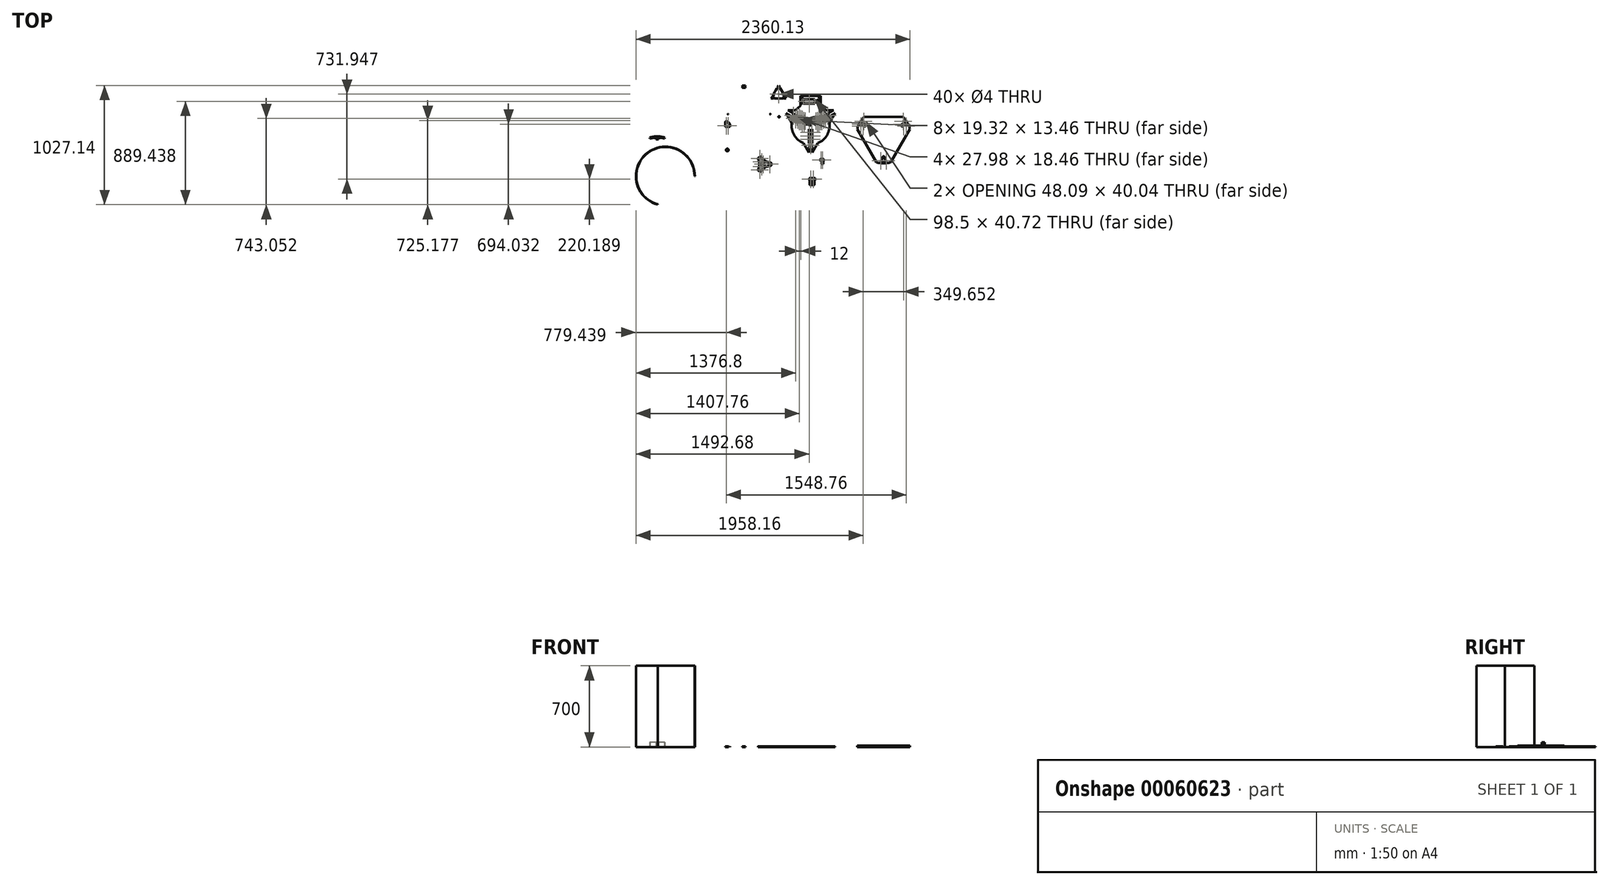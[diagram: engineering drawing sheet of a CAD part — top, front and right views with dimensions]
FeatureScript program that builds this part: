
annotation { "Feature Type Name" : "Feature", "Feature Type Description" : "" }
export const myFeature = defineFeature(function(context is Context, id is Id, definition is map)
    precondition{}
    {
        {
            var Q0;
            Q0=qCreatedBy(makeId("Top.planeOp"),FACE);
            var sketch = newSketch(context, id + "F0", { "sketchPlane" : qUnion([Q0])});
            skCircle(sketch, "E0", {"center": v(-448.83, 54.99) * mm, "radius": 1.5 * mm});
            skCircle(sketch, "E1", {"center": v(-448.8, 86.08) * mm, "radius": 1.5 * mm});
            skCircle(sketch, "E2", {"center": v(-453.84, -253.52) * mm, "radius": 11.5 * mm});
            skCircle(sketch, "E3", {"center": v(-386.12, -280.64) * mm, "radius": 2 * mm});
            skCircle(sketch, "E4", {"center": v(-423.42, -280.64) * mm, "radius": 2 * mm});
            skCircle(sketch, "E5", {"center": v(-469.5, -280.64) * mm, "radius": 2 * mm});
            skCircle(sketch, "E6", {"center": v(-438.44, -237.96) * mm, "radius": 1.5 * mm});
            skCircle(sketch, "E7", {"center": v(-469.53, -237.9) * mm, "radius": 1.5 * mm});
            skCircle(sketch, "E8", {"center": v(-439.73, -262.53) * mm, "radius": 1.5 * mm});
            skCircle(sketch, "E9", {"center": v(-448.28, -269) * mm, "radius": 1.5 * mm});
            skCircle(sketch, "E10", {"center": v(-438.44, -291.39) * mm, "radius": 1.5 * mm});
            skCircle(sketch, "E11", {"center": v(-469.55, -291.39) * mm, "radius": 1.5 * mm});
            skCircle(sketch, "E12", {"center": v(-469.55, -269) * mm, "radius": 1.5 * mm});
            skCircle(sketch, "E13", {"center": v(-83.7, 56.02) * mm, "radius": 2 * mm});
            skCircle(sketch, "E14", {"center": v(-231.13, -199.23) * mm, "radius": 2 * mm});
            skCircle(sketch, "E15", {"center": v(-378.53, 55.85) * mm, "radius": 2 * mm});
            skCircle(sketch, "E16", {"center": v(-231.13, -29.98) * mm, "radius": 177.5 * mm});
            skLineSegment(sketch, "E17", {"start": v(-11.84, 302.96) * mm, "end": v(-1.84, 285.64) * mm});
            skLineSegment(sketch, "E18", {"start": v(-1.84, 285.64) * mm, "end": v(-1.84, 258.8) * mm});
            skLineSegment(sketch, "E19", {"start": v(-1.84, 258.8) * mm, "end": v(2.16, 258.8) * mm});
            skLineSegment(sketch, "E20", {"start": v(2.16, 258.8) * mm, "end": v(2.16, 278.7) * mm});
            skLineSegment(sketch, "E21", {"start": v(2.16, 278.7) * mm, "end": v(39.1, 214.7) * mm});
            skLineSegment(sketch, "E22", {"start": v(39.1, 214.7) * mm, "end": v(21.87, 224.66) * mm});
            skLineSegment(sketch, "E23", {"start": v(21.87, 224.66) * mm, "end": v(19.87, 221.2) * mm});
            skLineSegment(sketch, "E24", {"start": v(19.87, 221.2) * mm, "end": v(43.1, 207.78) * mm});
            skLineSegment(sketch, "E25", {"start": v(43.1, 207.78) * mm, "end": v(53.1, 190.46) * mm});
            skLineSegment(sketch, "E26", {"start": v(53.1, 190.46) * mm, "end": v(33.1, 190.46) * mm});
            skLineSegment(sketch, "E27", {"start": v(33.1, 190.46) * mm, "end": v(9.87, 203.88) * mm});
            skLineSegment(sketch, "E28", {"start": v(9.87, 203.88) * mm, "end": v(7.87, 200.41) * mm});
            skLineSegment(sketch, "E29", {"start": v(7.87, 200.41) * mm, "end": v(25.1, 190.46) * mm});
            skLineSegment(sketch, "E30", {"start": v(25.1, 190.46) * mm, "end": v(-48.8, 190.46) * mm});
            skLineSegment(sketch, "E31", {"start": v(-48.8, 190.46) * mm, "end": v(-31.55, 200.41) * mm});
            skLineSegment(sketch, "E32", {"start": v(-31.55, 200.41) * mm, "end": v(-33.55, 203.88) * mm});
            skLineSegment(sketch, "E33", {"start": v(-33.55, 203.88) * mm, "end": v(-56.8, 190.46) * mm});
            skLineSegment(sketch, "E34", {"start": v(-56.8, 190.46) * mm, "end": v(-76.8, 190.46) * mm});
            skLineSegment(sketch, "E35", {"start": v(-76.8, 190.46) * mm, "end": v(-66.8, 207.78) * mm});
            skLineSegment(sketch, "E36", {"start": v(-66.8, 207.78) * mm, "end": v(-43.55, 221.2) * mm});
            skLineSegment(sketch, "E37", {"start": v(-43.55, 221.2) * mm, "end": v(-45.55, 224.66) * mm});
            skLineSegment(sketch, "E38", {"start": v(-45.55, 224.66) * mm, "end": v(-62.8, 214.7) * mm});
            skLineSegment(sketch, "E39", {"start": v(-62.8, 214.7) * mm, "end": v(-25.84, 278.7) * mm});
            skLineSegment(sketch, "E40", {"start": v(-25.84, 278.7) * mm, "end": v(-25.84, 258.8) * mm});
            skLineSegment(sketch, "E41", {"start": v(-25.84, 258.8) * mm, "end": v(-21.84, 258.8) * mm});
            skLineSegment(sketch, "E42", {"start": v(-21.84, 258.8) * mm, "end": v(-21.84, 285.64) * mm});
            skLineSegment(sketch, "E43", {"start": v(-21.84, 285.64) * mm, "end": v(-11.84, 302.96) * mm});
            skLineSegment(sketch, "E44", {"start": v(-314.86, 291.44) * mm, "end": v(-314.86, 289.44) * mm});
            skLineSegment(sketch, "E45", {"start": v(-314.86, 289.44) * mm, "end": v(-318.06, 289.45) * mm});
            skLineSegment(sketch, "E46", {"start": v(-318.06, 289.45) * mm, "end": v(-318.06, 291.45) * mm});
            skLineSegment(sketch, "E47", {"start": v(-318.06, 291.45) * mm, "end": v(-321.05, 291.44) * mm});
            skLineSegment(sketch, "E48", {"start": v(-321.05, 291.44) * mm, "end": v(-321.05, 287.57) * mm});
            skLineSegment(sketch, "E49", {"start": v(-325, 287.57) * mm, "end": v(-325, 282.96) * mm});
            skLineSegment(sketch, "E50", {"start": v(-314.88, 291.44) * mm, "end": v(-314.86, 291.44) * mm});
            skLineSegment(sketch, "E51", {"start": v(-314.86, 291.44) * mm, "end": v(-312.83, 291.44) * mm});
            skLineSegment(sketch, "E52", {"start": v(-312.83, 291.44) * mm, "end": v(-312.83, 294.44) * mm});
            skLineSegment(sketch, "E53", {"start": v(-312.83, 294.44) * mm, "end": v(-314.81, 294.44) * mm});
            skLineSegment(sketch, "E54", {"start": v(-314.81, 294.44) * mm, "end": v(-314.86, 294.44) * mm});
            skLineSegment(sketch, "E55", {"start": v(-314.86, 294.44) * mm, "end": v(-314.86, 296.44) * mm});
            skLineSegment(sketch, "E56", {"start": v(-314.86, 296.44) * mm, "end": v(-318.06, 296.45) * mm});
            skLineSegment(sketch, "E57", {"start": v(-318.06, 296.45) * mm, "end": v(-318.06, 294.44) * mm});
            skLineSegment(sketch, "E58", {"start": v(-318.06, 294.44) * mm, "end": v(-321.05, 294.44) * mm});
            skLineSegment(sketch, "E59", {"start": v(-321.05, 294.44) * mm, "end": v(-321.05, 298.32) * mm});
            skLineSegment(sketch, "E60", {"start": v(-321.05, 298.32) * mm, "end": v(-325, 298.32) * mm});
            skLineSegment(sketch, "E61", {"start": v(-325, 298.32) * mm, "end": v(-325, 302.96) * mm});
            skLineSegment(sketch, "E62", {"start": v(-461.5, -205.94) * mm, "end": v(-452.17, -195.94) * mm});
            skLineSegment(sketch, "E63", {"start": v(-452.17, -195.94) * mm, "end": v(-452, -195.94) * mm});
            skLineSegment(sketch, "E64", {"start": v(-452, -195.94) * mm, "end": v(-451.98, -195.73) * mm});
            skLineSegment(sketch, "E65", {"start": v(-451.98, -195.73) * mm, "end": v(-447.3, -190.7) * mm});
            skLineSegment(sketch, "E66", {"start": v(-447.3, -190.7) * mm, "end": v(-442.5, -195.94) * mm});
            skLineSegment(sketch, "E67", {"start": v(-442.5, -195.94) * mm, "end": v(-452, -205.94) * mm});
            skLineSegment(sketch, "E68", {"start": v(-452, -205.94) * mm, "end": v(-461.5, -205.94) * mm});
            skLineSegment(sketch, "E69", {"start": v(-442.5, -144.44) * mm, "end": v(-447.25, -149.62) * mm});
            skLineSegment(sketch, "E70", {"start": v(-447.25, -149.62) * mm, "end": v(-456.75, -149.62) * mm});
            skLineSegment(sketch, "E71", {"start": v(-456.75, -149.62) * mm, "end": v(-461.5, -144.44) * mm});
            skLineSegment(sketch, "E72", {"start": v(-461.5, -144.44) * mm, "end": v(-452, -144.44) * mm});
            skLineSegment(sketch, "E73", {"start": v(-452, -144.44) * mm, "end": v(-461.5, -134.44) * mm});
            skLineSegment(sketch, "E74", {"start": v(-461.5, -134.44) * mm, "end": v(-456.7, -129.2) * mm});
            skLineSegment(sketch, "E75", {"start": v(-456.7, -129.2) * mm, "end": v(-442.5, -144.44) * mm});
            skLineSegment(sketch, "E76", {"start": v(-442.5, -113.69) * mm, "end": v(-447.3, -118.92) * mm});
            skLineSegment(sketch, "E77", {"start": v(-447.3, -118.92) * mm, "end": v(-461.5, -103.69) * mm});
            skLineSegment(sketch, "E78", {"start": v(-461.5, -103.69) * mm, "end": v(-451.82, -103.69) * mm});
            skLineSegment(sketch, "E79", {"start": v(-451.82, -103.69) * mm, "end": v(-442.5, -113.69) * mm});
            skLineSegment(sketch, "E80", {"start": v(-461.5, -175.19) * mm, "end": v(-452, -165.19) * mm});
            skLineSegment(sketch, "E81", {"start": v(-452, -165.19) * mm, "end": v(-461.5, -165.19) * mm});
            skLineSegment(sketch, "E82", {"start": v(-461.5, -165.19) * mm, "end": v(-456.75, -160) * mm});
            skLineSegment(sketch, "E83", {"start": v(-456.75, -160) * mm, "end": v(-447.34, -160) * mm});
            skLineSegment(sketch, "E84", {"start": v(-447.34, -160) * mm, "end": v(-442.67, -165.19) * mm});
            skLineSegment(sketch, "E85", {"start": v(-442.67, -165.19) * mm, "end": v(-456.73, -180.4) * mm});
            skLineSegment(sketch, "E86", {"start": v(-456.73, -180.4) * mm, "end": v(-461.5, -175.19) * mm});
            skLineSegment(sketch, "E87", {"start": v(-465.48, -225.19) * mm, "end": v(-469.48, -225.19) * mm});
            skLineSegment(sketch, "E88", {"start": v(-465.48, -205.19) * mm, "end": v(-469.48, -205.19) * mm});
            skLineSegment(sketch, "E89", {"start": v(-469.48, -205.19) * mm, "end": v(-469.48, -209.84) * mm});
            skLineSegment(sketch, "E90", {"start": v(-469.48, -209.84) * mm, "end": v(-465.48, -209.84) * mm});
            skLineSegment(sketch, "E91", {"start": v(-465.48, -209.84) * mm, "end": v(-465.48, -205.19) * mm});
            skLineSegment(sketch, "E92", {"start": v(-465.48, -225.19) * mm, "end": v(-465.48, -220.59) * mm});
            skLineSegment(sketch, "E93", {"start": v(-465.48, -220.59) * mm, "end": v(-469.48, -220.59) * mm});
            skLineSegment(sketch, "E94", {"start": v(-469.48, -220.59) * mm, "end": v(-469.48, -225.19) * mm});
            skLineSegment(sketch, "E95", {"start": v(-465.57, -172.33) * mm, "end": v(-469.57, -172.33) * mm});
            skLineSegment(sketch, "E96", {"start": v(-465.57, -152.33) * mm, "end": v(-469.57, -152.33) * mm});
            skLineSegment(sketch, "E97", {"start": v(-469.57, -152.33) * mm, "end": v(-469.57, -156.98) * mm});
            skLineSegment(sketch, "E98", {"start": v(-469.57, -156.98) * mm, "end": v(-465.57, -156.98) * mm});
            skLineSegment(sketch, "E99", {"start": v(-465.57, -156.98) * mm, "end": v(-465.57, -152.33) * mm});
            skLineSegment(sketch, "E100", {"start": v(-465.57, -172.33) * mm, "end": v(-465.57, -167.73) * mm});
            skLineSegment(sketch, "E101", {"start": v(-465.57, -167.73) * mm, "end": v(-469.57, -167.73) * mm});
            skLineSegment(sketch, "E102", {"start": v(-469.57, -167.73) * mm, "end": v(-469.57, -172.33) * mm});
            skLineSegment(sketch, "E103", {"start": v(-439.62, -125.5) * mm, "end": v(-439.58, -125.5) * mm});
            skLineSegment(sketch, "E104", {"start": v(-439.58, -125.5) * mm, "end": v(-439.2, -125.56) * mm});
            skLineSegment(sketch, "E105", {"start": v(-439.2, -125.56) * mm, "end": v(-439.19, -127.56) * mm});
            skLineSegment(sketch, "E106", {"start": v(-439.19, -127.56) * mm, "end": v(-435.99, -127.56) * mm});
            skLineSegment(sketch, "E107", {"start": v(-435.99, -127.56) * mm, "end": v(-436, -125.56) * mm});
            skLineSegment(sketch, "E108", {"start": v(-436, -125.56) * mm, "end": v(-433, -125.56) * mm});
            skLineSegment(sketch, "E109", {"start": v(-433, -125.56) * mm, "end": v(-433, -129.44) * mm});
            skLineSegment(sketch, "E110", {"start": v(-433, -129.44) * mm, "end": v(-429, -129.44) * mm});
            skLineSegment(sketch, "E111", {"start": v(-429, -129.44) * mm, "end": v(-429, -149.44) * mm});
            skLineSegment(sketch, "E112", {"start": v(-429, -149.44) * mm, "end": v(-433, -149.44) * mm});
            skLineSegment(sketch, "E113", {"start": v(-433, -149.44) * mm, "end": v(-433, -153.31) * mm});
            skLineSegment(sketch, "E114", {"start": v(-433, -153.31) * mm, "end": v(-435.97, -153.31) * mm});
            skLineSegment(sketch, "E115", {"start": v(-435.97, -153.31) * mm, "end": v(-435.97, -151.31) * mm});
            skLineSegment(sketch, "E116", {"start": v(-435.97, -151.31) * mm, "end": v(-439.17, -151.31) * mm});
            skLineSegment(sketch, "E117", {"start": v(-439.17, -151.31) * mm, "end": v(-439.17, -153.3) * mm});
            skLineSegment(sketch, "E118", {"start": v(-439.24, -156.3) * mm, "end": v(-439.17, -156.3) * mm});
            skLineSegment(sketch, "E119", {"start": v(-439.17, -156.3) * mm, "end": v(-439.16, -158.31) * mm});
            skLineSegment(sketch, "E120", {"start": v(-439.16, -158.31) * mm, "end": v(-435.96, -158.31) * mm});
            skLineSegment(sketch, "E121", {"start": v(-435.96, -158.31) * mm, "end": v(-435.97, -156.3) * mm});
            skLineSegment(sketch, "E122", {"start": v(-435.97, -156.3) * mm, "end": v(-433, -156.31) * mm});
            skLineSegment(sketch, "E123", {"start": v(-433, -156.31) * mm, "end": v(-433, -160.19) * mm});
            skLineSegment(sketch, "E124", {"start": v(-433, -160.19) * mm, "end": v(-429, -160.19) * mm});
            skLineSegment(sketch, "E125", {"start": v(-429, -160.19) * mm, "end": v(-429, -180.19) * mm});
            skLineSegment(sketch, "E126", {"start": v(-429, -180.19) * mm, "end": v(-433, -180.19) * mm});
            skLineSegment(sketch, "E127", {"start": v(-433, -180.19) * mm, "end": v(-433, -184.06) * mm});
            skLineSegment(sketch, "E128", {"start": v(-433, -184.06) * mm, "end": v(-435.94, -184.06) * mm});
            skLineSegment(sketch, "E129", {"start": v(-435.94, -184.06) * mm, "end": v(-435.94, -182.06) * mm});
            skLineSegment(sketch, "E130", {"start": v(-435.94, -182.06) * mm, "end": v(-439.14, -182.06) * mm});
            skLineSegment(sketch, "E131", {"start": v(-439.14, -182.06) * mm, "end": v(-439.14, -184.06) * mm});
            skLineSegment(sketch, "E132", {"start": v(-439.14, -184.06) * mm, "end": v(-439.18, -184.07) * mm});
            skLineSegment(sketch, "E133", {"start": v(-439.14, -187.07) * mm, "end": v(-439.14, -189.06) * mm});
            skLineSegment(sketch, "E134", {"start": v(-439.14, -189.06) * mm, "end": v(-435.94, -189.06) * mm});
            skLineSegment(sketch, "E135", {"start": v(-435.94, -189.06) * mm, "end": v(-435.94, -187.06) * mm});
            skLineSegment(sketch, "E136", {"start": v(-435.94, -187.06) * mm, "end": v(-433, -187.06) * mm});
            skLineSegment(sketch, "E137", {"start": v(-433, -187.06) * mm, "end": v(-433, -190.94) * mm});
            skLineSegment(sketch, "E138", {"start": v(-433, -190.94) * mm, "end": v(-429, -190.94) * mm});
            skLineSegment(sketch, "E139", {"start": v(-429, -190.94) * mm, "end": v(-429, -220.94) * mm});
            skLineSegment(sketch, "E140", {"start": v(-429, -220.94) * mm, "end": v(-433, -220.94) * mm});
            skLineSegment(sketch, "E141", {"start": v(-433, -220.94) * mm, "end": v(-433, -230.82) * mm});
            skLineSegment(sketch, "E142", {"start": v(-433, -230.82) * mm, "end": v(-429, -230.82) * mm});
            skLineSegment(sketch, "E143", {"start": v(-429, -230.82) * mm, "end": v(-429, -238.82) * mm});
            skLineSegment(sketch, "E144", {"start": v(-429, -238.82) * mm, "end": v(-433, -238.82) * mm});
            skLineSegment(sketch, "E145", {"start": v(-433, -238.82) * mm, "end": v(-433, -249.24) * mm});
            skLineSegment(sketch, "E146", {"start": v(-433, -249.24) * mm, "end": v(-429, -249.24) * mm});
            skLineSegment(sketch, "E147", {"start": v(-429, -249.24) * mm, "end": v(-429, -257.24) * mm});
            skLineSegment(sketch, "E148", {"start": v(-429, -257.24) * mm, "end": v(-373, -270.43) * mm});
            skLineSegment(sketch, "E149", {"start": v(-373, -270.43) * mm, "end": v(-373, -290.43) * mm});
            skLineSegment(sketch, "E150", {"start": v(-373, -290.43) * mm, "end": v(-433, -302.96) * mm});
            skLineSegment(sketch, "E151", {"start": v(-433, -302.96) * mm, "end": v(-475, -302.96) * mm});
            skLineSegment(sketch, "E152", {"start": v(-475, -302.96) * mm, "end": v(-475, -95.5) * mm});
            skLineSegment(sketch, "E153", {"start": v(-475, -95.5) * mm, "end": v(-468.83, -95.5) * mm});
            skLineSegment(sketch, "E154", {"start": v(-468.83, -95.5) * mm, "end": v(-468.83, -106.93) * mm});
            skLineSegment(sketch, "E155", {"start": v(-468.83, -106.93) * mm, "end": v(-464.83, -106.93) * mm});
            skLineSegment(sketch, "E156", {"start": v(-464.83, -106.93) * mm, "end": v(-464.83, -95.5) * mm});
            skLineSegment(sketch, "E157", {"start": v(-464.83, -95.5) * mm, "end": v(-429, -95.5) * mm});
            skLineSegment(sketch, "E158", {"start": v(-429, -95.5) * mm, "end": v(-429, -118.69) * mm});
            skLineSegment(sketch, "E159", {"start": v(-429, -118.69) * mm, "end": v(-433, -118.69) * mm});
            skLineSegment(sketch, "E160", {"start": v(-433, -118.69) * mm, "end": v(-433, -122.56) * mm});
            skLineSegment(sketch, "E161", {"start": v(-433, -122.56) * mm, "end": v(-436, -122.56) * mm});
            skLineSegment(sketch, "E162", {"start": v(-436, -122.56) * mm, "end": v(-436, -120.56) * mm});
            skLineSegment(sketch, "E163", {"start": v(-436, -120.56) * mm, "end": v(-439.2, -120.56) * mm});
            skLineSegment(sketch, "E164", {"start": v(-439.2, -120.56) * mm, "end": v(-439.2, -122.56) * mm});
            skLineSegment(sketch, "E165", {"start": v(-439.2, -122.56) * mm, "end": v(-439.2, -122.56) * mm});
            skLineSegment(sketch, "E166", {"start": v(-439.18, -184.07) * mm, "end": v(-440.73, -184.07) * mm});
            skLineSegment(sketch, "E167", {"start": v(-440.73, -184.07) * mm, "end": v(-440.73, -187.07) * mm});
            skLineSegment(sketch, "E168", {"start": v(-440.73, -187.07) * mm, "end": v(-439.14, -187.07) * mm});
            skLineSegment(sketch, "E169", {"start": v(-439.2, -122.56) * mm, "end": v(-439.2, -122.5) * mm});
            skLineSegment(sketch, "E170", {"start": v(-439.2, -122.5) * mm, "end": v(-440.8, -122.5) * mm});
            skLineSegment(sketch, "E171", {"start": v(-440.8, -122.5) * mm, "end": v(-440.8, -125.5) * mm});
            skLineSegment(sketch, "E172", {"start": v(-440.8, -125.5) * mm, "end": v(-439.62, -125.5) * mm});
            skLineSegment(sketch, "E173", {"start": v(-439.17, -153.3) * mm, "end": v(-440.77, -153.3) * mm});
            skLineSegment(sketch, "E174", {"start": v(-440.77, -153.3) * mm, "end": v(-440.77, -156.3) * mm});
            skLineSegment(sketch, "E175", {"start": v(-440.77, -156.3) * mm, "end": v(-439.24, -156.3) * mm});
            skCircle(sketch, "E176", {"center": v(-452, -185.57) * mm, "radius": 4.5 * mm});
            skCircle(sketch, "E177", {"center": v(-452, -124) * mm, "radius": 4.5 * mm});
            skCircle(sketch, "E178", {"center": v(-467.5, -214.97) * mm, "radius": 1.5 * mm});
            skEllipse(sketch, "E179", {"center": v(-452.09, -222.76) * mm, "majorRadius": 9.41 * mm, "minorRadius": 1.97 * mm, "majorAxis": v(1, 0)});
            skCircle(sketch, "E180", {"center": v(-467.57, -162.23) * mm, "radius": 1.5 * mm});
            skEllipse(sketch, "E181", {"center": v(-455, -297.5) * mm, "majorRadius": 9.41 * mm, "minorRadius": 1.97 * mm, "majorAxis": v(1, 0)});
            skLineSegment(sketch, "E182", {"start": v(-451.93, 91.53) * mm, "end": v(-442.71, 91.53) * mm});
            skLineSegment(sketch, "E183", {"start": v(-442.75, 91.53) * mm, "end": v(-448.2, 71.57) * mm});
            skLineSegment(sketch, "E184", {"start": v(-448.2, 71.57) * mm, "end": v(-442.75, 49.53) * mm});
            skLineSegment(sketch, "E185", {"start": v(-442.71, 49.53) * mm, "end": v(-451.93, 49.53) * mm});
            skLineSegment(sketch, "E186", {"start": v(-451.84, 49.53) * mm, "end": v(-457.28, 71.57) * mm});
            skLineSegment(sketch, "E187", {"start": v(-457.28, 71.57) * mm, "end": v(-451.84, 91.53) * mm});
            skLineSegment(sketch, "E188", {"start": v(-431.84, -33.47) * mm, "end": v(-431.84, -53.47) * mm});
            skLineSegment(sketch, "E189", {"start": v(-471.84, -53.47) * mm, "end": v(-471.84, -13.47) * mm});
            skLineSegment(sketch, "E190", {"start": v(-471.84, -13.47) * mm, "end": v(-471.83, -13.37) * mm});
            skLineSegment(sketch, "E191", {"start": v(421.7, 33.58) * mm, "end": v(419.7, 37.04) * mm});
            skLineSegment(sketch, "E192", {"start": v(419.7, 37.04) * mm, "end": v(412.77, 33.04) * mm});
            skLineSegment(sketch, "E193", {"start": v(412.77, 33.04) * mm, "end": v(414.77, 29.58) * mm});
            skLineSegment(sketch, "E194", {"start": v(414.77, 29.58) * mm, "end": v(421.7, 33.58) * mm});
            skLineSegment(sketch, "E195", {"start": v(277.88, -207.54) * mm, "end": v(273.88, -207.54) * mm});
            skLineSegment(sketch, "E196", {"start": v(273.88, -207.54) * mm, "end": v(273.88, -215.54) * mm});
            skLineSegment(sketch, "E197", {"start": v(273.88, -215.54) * mm, "end": v(277.88, -215.54) * mm});
            skLineSegment(sketch, "E198", {"start": v(277.88, -215.54) * mm, "end": v(277.88, -207.54) * mm});
            skLineSegment(sketch, "E199", {"start": v(120.05, 57.83) * mm, "end": v(118.05, 54.36) * mm});
            skLineSegment(sketch, "E200", {"start": v(118.05, 54.36) * mm, "end": v(124.98, 50.36) * mm});
            skLineSegment(sketch, "E201", {"start": v(124.98, 50.36) * mm, "end": v(126.98, 53.83) * mm});
            skLineSegment(sketch, "E202", {"start": v(126.98, 53.83) * mm, "end": v(120.05, 57.83) * mm});
            skLineSegment(sketch, "E203", {"start": v(214.77, 3.14) * mm, "end": v(197.45, 13.14) * mm});
            skLineSegment(sketch, "E204", {"start": v(197.45, 13.14) * mm, "end": v(195.45, 9.67) * mm});
            skLineSegment(sketch, "E205", {"start": v(195.45, 9.67) * mm, "end": v(212.77, -0.33) * mm});
            skLineSegment(sketch, "E206", {"start": v(212.77, -0.33) * mm, "end": v(214.77, 3.14) * mm});
            skLineSegment(sketch, "E207", {"start": v(224.08, -2.24) * mm, "end": v(222.08, -5.7) * mm});
            skLineSegment(sketch, "E208", {"start": v(222.08, -5.7) * mm, "end": v(242.17, -17.3) * mm});
            skLineSegment(sketch, "E209", {"start": v(242.17, -17.3) * mm, "end": v(244.17, -13.83) * mm});
            skLineSegment(sketch, "E210", {"start": v(244.17, -13.83) * mm, "end": v(224.08, -2.24) * mm});
            skLineSegment(sketch, "E211", {"start": v(212.08, -23.02) * mm, "end": v(210.08, -26.49) * mm});
            skLineSegment(sketch, "E212", {"start": v(210.08, -26.49) * mm, "end": v(230.17, -38.08) * mm});
            skLineSegment(sketch, "E213", {"start": v(230.17, -38.08) * mm, "end": v(232.17, -34.62) * mm});
            skLineSegment(sketch, "E214", {"start": v(232.17, -34.62) * mm, "end": v(212.08, -23.02) * mm});
            skLineSegment(sketch, "E215", {"start": v(185.45, -7.65) * mm, "end": v(183.45, -11.11) * mm});
            skLineSegment(sketch, "E216", {"start": v(183.45, -11.11) * mm, "end": v(200.77, -21.11) * mm});
            skLineSegment(sketch, "E217", {"start": v(200.77, -21.11) * mm, "end": v(202.77, -17.65) * mm});
            skLineSegment(sketch, "E218", {"start": v(202.77, -17.65) * mm, "end": v(185.45, -7.65) * mm});
            skLineSegment(sketch, "E219", {"start": v(174.14, -5.74) * mm, "end": v(176.14, -2.27) * mm});
            skLineSegment(sketch, "E220", {"start": v(176.14, -2.27) * mm, "end": v(158.82, 7.73) * mm});
            skLineSegment(sketch, "E221", {"start": v(158.82, 7.73) * mm, "end": v(156.82, 4.26) * mm});
            skLineSegment(sketch, "E222", {"start": v(156.82, 4.26) * mm, "end": v(174.14, -5.74) * mm});
            skLineSegment(sketch, "E223", {"start": v(188.14, 18.51) * mm, "end": v(170.82, 28.51) * mm});
            skLineSegment(sketch, "E224", {"start": v(170.82, 28.51) * mm, "end": v(168.82, 25.05) * mm});
            skLineSegment(sketch, "E225", {"start": v(168.82, 25.05) * mm, "end": v(186.14, 15.05) * mm});
            skLineSegment(sketch, "E226", {"start": v(186.14, 15.05) * mm, "end": v(188.14, 18.51) * mm});
            skLineSegment(sketch, "E227", {"start": v(161.51, 33.89) * mm, "end": v(135.53, 48.89) * mm});
            skLineSegment(sketch, "E228", {"start": v(135.53, 48.89) * mm, "end": v(133.53, 45.42) * mm});
            skLineSegment(sketch, "E229", {"start": v(133.53, 45.42) * mm, "end": v(159.51, 30.42) * mm});
            skLineSegment(sketch, "E230", {"start": v(159.51, 30.42) * mm, "end": v(161.51, 33.89) * mm});
            skLineSegment(sketch, "E231", {"start": v(149.51, 13.1) * mm, "end": v(123.53, 28.1) * mm});
            skLineSegment(sketch, "E232", {"start": v(123.53, 28.1) * mm, "end": v(121.53, 24.64) * mm});
            skLineSegment(sketch, "E233", {"start": v(121.53, 24.64) * mm, "end": v(147.51, 9.64) * mm});
            skLineSegment(sketch, "E234", {"start": v(147.51, 9.64) * mm, "end": v(149.51, 13.1) * mm});
            skLineSegment(sketch, "E235", {"start": v(249.88, -95.4) * mm, "end": v(253.88, -95.4) * mm});
            skLineSegment(sketch, "E236", {"start": v(253.88, -95.4) * mm, "end": v(253.88, -72.21) * mm});
            skLineSegment(sketch, "E237", {"start": v(253.88, -72.21) * mm, "end": v(249.88, -72.21) * mm});
            skLineSegment(sketch, "E238", {"start": v(249.88, -72.21) * mm, "end": v(249.88, -95.4) * mm});
            skLineSegment(sketch, "E239", {"start": v(273.88, -95.4) * mm, "end": v(277.88, -95.4) * mm});
            skLineSegment(sketch, "E240", {"start": v(277.88, -95.4) * mm, "end": v(277.88, -72.21) * mm});
            skLineSegment(sketch, "E241", {"start": v(277.88, -72.21) * mm, "end": v(273.88, -72.21) * mm});
            skLineSegment(sketch, "E242", {"start": v(273.88, -72.21) * mm, "end": v(273.88, -95.4) * mm});
            skLineSegment(sketch, "E243", {"start": v(273.88, -126.16) * mm, "end": v(277.88, -126.16) * mm});
            skLineSegment(sketch, "E244", {"start": v(277.88, -126.16) * mm, "end": v(277.88, -106.16) * mm});
            skLineSegment(sketch, "E245", {"start": v(277.88, -106.16) * mm, "end": v(273.88, -106.16) * mm});
            skLineSegment(sketch, "E246", {"start": v(273.88, -106.16) * mm, "end": v(273.88, -126.16) * mm});
            skLineSegment(sketch, "E247", {"start": v(249.88, -126.16) * mm, "end": v(253.88, -126.16) * mm});
            skLineSegment(sketch, "E248", {"start": v(253.88, -126.16) * mm, "end": v(253.88, -106.16) * mm});
            skLineSegment(sketch, "E249", {"start": v(253.88, -106.16) * mm, "end": v(249.88, -106.16) * mm});
            skLineSegment(sketch, "E250", {"start": v(249.88, -106.16) * mm, "end": v(249.88, -126.16) * mm});
            skLineSegment(sketch, "E251", {"start": v(253.88, -136.9) * mm, "end": v(249.88, -136.9) * mm});
            skLineSegment(sketch, "E252", {"start": v(249.88, -136.9) * mm, "end": v(249.88, -156.9) * mm});
            skLineSegment(sketch, "E253", {"start": v(249.88, -156.9) * mm, "end": v(253.88, -156.9) * mm});
            skLineSegment(sketch, "E254", {"start": v(253.88, -156.9) * mm, "end": v(253.88, -136.9) * mm});
            skLineSegment(sketch, "E255", {"start": v(277.88, -136.9) * mm, "end": v(273.88, -136.9) * mm});
            skLineSegment(sketch, "E256", {"start": v(273.88, -136.9) * mm, "end": v(273.88, -156.9) * mm});
            skLineSegment(sketch, "E257", {"start": v(273.88, -156.9) * mm, "end": v(277.88, -156.9) * mm});
            skLineSegment(sketch, "E258", {"start": v(277.88, -156.9) * mm, "end": v(277.88, -136.9) * mm});
            skLineSegment(sketch, "E259", {"start": v(277.88, -167.66) * mm, "end": v(273.88, -167.66) * mm});
            skLineSegment(sketch, "E260", {"start": v(273.88, -167.66) * mm, "end": v(273.88, -197.66) * mm});
            skLineSegment(sketch, "E261", {"start": v(273.88, -197.66) * mm, "end": v(277.88, -197.66) * mm});
            skLineSegment(sketch, "E262", {"start": v(277.88, -197.66) * mm, "end": v(277.88, -167.66) * mm});
            skLineSegment(sketch, "E263", {"start": v(253.88, -167.66) * mm, "end": v(249.88, -167.66) * mm});
            skLineSegment(sketch, "E264", {"start": v(249.88, -167.66) * mm, "end": v(249.88, -197.66) * mm});
            skLineSegment(sketch, "E265", {"start": v(249.88, -197.66) * mm, "end": v(253.88, -197.66) * mm});
            skLineSegment(sketch, "E266", {"start": v(253.88, -197.66) * mm, "end": v(253.88, -167.66) * mm});
            skLineSegment(sketch, "E267", {"start": v(351.6, -2.27) * mm, "end": v(353.6, -5.74) * mm});
            skLineSegment(sketch, "E268", {"start": v(353.6, -5.74) * mm, "end": v(370.93, 4.26) * mm});
            skLineSegment(sketch, "E269", {"start": v(370.93, 4.26) * mm, "end": v(368.93, 7.73) * mm});
            skLineSegment(sketch, "E270", {"start": v(368.93, 7.73) * mm, "end": v(351.6, -2.27) * mm});
            skLineSegment(sketch, "E271", {"start": v(366.24, 33.89) * mm, "end": v(368.24, 30.42) * mm});
            skLineSegment(sketch, "E272", {"start": v(368.24, 30.42) * mm, "end": v(394.22, 45.42) * mm});
            skLineSegment(sketch, "E273", {"start": v(394.22, 45.42) * mm, "end": v(392.22, 48.89) * mm});
            skLineSegment(sketch, "E274", {"start": v(392.22, 48.89) * mm, "end": v(366.24, 33.89) * mm});
            skLineSegment(sketch, "E275", {"start": v(339.6, 18.51) * mm, "end": v(341.6, 15.05) * mm});
            skLineSegment(sketch, "E276", {"start": v(341.6, 15.05) * mm, "end": v(358.93, 25.05) * mm});
            skLineSegment(sketch, "E277", {"start": v(358.93, 25.05) * mm, "end": v(356.93, 28.51) * mm});
            skLineSegment(sketch, "E278", {"start": v(356.93, 28.51) * mm, "end": v(339.6, 18.51) * mm});
            skLineSegment(sketch, "E279", {"start": v(312.98, 3.14) * mm, "end": v(314.98, -0.33) * mm});
            skLineSegment(sketch, "E280", {"start": v(314.98, -0.33) * mm, "end": v(332.3, 9.67) * mm});
            skLineSegment(sketch, "E281", {"start": v(332.3, 9.67) * mm, "end": v(330.3, 13.14) * mm});
            skLineSegment(sketch, "E282", {"start": v(330.3, 13.14) * mm, "end": v(312.98, 3.14) * mm});
            skLineSegment(sketch, "E283", {"start": v(324.98, -17.65) * mm, "end": v(326.98, -21.11) * mm});
            skLineSegment(sketch, "E284", {"start": v(326.98, -21.11) * mm, "end": v(344.3, -11.11) * mm});
            skLineSegment(sketch, "E285", {"start": v(344.3, -11.11) * mm, "end": v(342.3, -7.65) * mm});
            skLineSegment(sketch, "E286", {"start": v(342.3, -7.65) * mm, "end": v(324.98, -17.65) * mm});
            skLineSegment(sketch, "E287", {"start": v(303.67, -2.24) * mm, "end": v(283.58, -13.83) * mm});
            skLineSegment(sketch, "E288", {"start": v(283.58, -13.83) * mm, "end": v(285.58, -17.3) * mm});
            skLineSegment(sketch, "E289", {"start": v(285.58, -17.3) * mm, "end": v(305.67, -5.7) * mm});
            skLineSegment(sketch, "E290", {"start": v(305.67, -5.7) * mm, "end": v(303.67, -2.24) * mm});
            skLineSegment(sketch, "E291", {"start": v(315.67, -23.02) * mm, "end": v(295.58, -34.62) * mm});
            skLineSegment(sketch, "E292", {"start": v(295.58, -34.62) * mm, "end": v(297.58, -38.08) * mm});
            skLineSegment(sketch, "E293", {"start": v(297.58, -38.08) * mm, "end": v(317.67, -26.49) * mm});
            skLineSegment(sketch, "E294", {"start": v(317.67, -26.49) * mm, "end": v(315.67, -23.02) * mm});
            skLineSegment(sketch, "E295", {"start": v(400.77, 53.83) * mm, "end": v(402.77, 50.36) * mm});
            skLineSegment(sketch, "E296", {"start": v(402.77, 50.36) * mm, "end": v(409.7, 54.36) * mm});
            skLineSegment(sketch, "E297", {"start": v(409.7, 54.36) * mm, "end": v(407.7, 57.83) * mm});
            skLineSegment(sketch, "E298", {"start": v(407.7, 57.83) * mm, "end": v(400.77, 53.83) * mm});
            skLineSegment(sketch, "E299", {"start": v(404.22, 28.1) * mm, "end": v(378.24, 13.1) * mm});
            skLineSegment(sketch, "E300", {"start": v(378.24, 13.1) * mm, "end": v(380.24, 9.64) * mm});
            skLineSegment(sketch, "E301", {"start": v(380.24, 9.64) * mm, "end": v(406.22, 24.64) * mm});
            skLineSegment(sketch, "E302", {"start": v(406.22, 24.64) * mm, "end": v(404.22, 28.1) * mm});
            skLineSegment(sketch, "E303", {"start": v(112.98, 29.58) * mm, "end": v(114.98, 33.04) * mm});
            skLineSegment(sketch, "E304", {"start": v(114.98, 33.04) * mm, "end": v(108.05, 37.04) * mm});
            skLineSegment(sketch, "E305", {"start": v(108.05, 37.04) * mm, "end": v(106.05, 33.58) * mm});
            skLineSegment(sketch, "E306", {"start": v(106.05, 33.58) * mm, "end": v(112.98, 29.58) * mm});
            skLineSegment(sketch, "E307", {"start": v(66.75, 88.6) * mm, "end": v(131.72, 88.6) * mm});
            skLineSegment(sketch, "E308", {"start": v(461, 88.6) * mm, "end": v(416.73, 63.04) * mm});
            skLineSegment(sketch, "E309", {"start": v(416.73, 63.04) * mm, "end": v(418.73, 59.58) * mm});
            skLineSegment(sketch, "E310", {"start": v(412.63, 56.05) * mm, "end": v(422.62, 38.73) * mm});
            skLineSegment(sketch, "E311", {"start": v(428.73, 42.26) * mm, "end": v(430.73, 38.8) * mm});
            skLineSegment(sketch, "E312", {"start": v(430.73, 38.8) * mm, "end": v(475, 64.35) * mm});
            skLineSegment(sketch, "E313", {"start": v(475, 64.35) * mm, "end": v(426.76, -19.2) * mm});
            skLineSegment(sketch, "E314", {"start": v(326.1, -193.53) * mm, "end": v(277.88, -277.08) * mm});
            skLineSegment(sketch, "E315", {"start": v(277.88, -277.08) * mm, "end": v(277.88, -225.96) * mm});
            skLineSegment(sketch, "E316", {"start": v(277.88, -225.96) * mm, "end": v(273.88, -225.96) * mm});
            skLineSegment(sketch, "E317", {"start": v(273.88, -218.91) * mm, "end": v(253.88, -218.91) * mm});
            skLineSegment(sketch, "E318", {"start": v(253.88, -225.96) * mm, "end": v(249.88, -225.96) * mm});
            skLineSegment(sketch, "E319", {"start": v(249.88, -225.96) * mm, "end": v(249.88, -277.08) * mm});
            skLineSegment(sketch, "E320", {"start": v(249.88, -277.08) * mm, "end": v(201.64, -193.53) * mm});
            skLineSegment(sketch, "E321", {"start": v(100.99, -19.2) * mm, "end": v(52.75, 64.35) * mm});
            skLineSegment(sketch, "E322", {"start": v(52.75, 64.35) * mm, "end": v(97.02, 38.8) * mm});
            skLineSegment(sketch, "E323", {"start": v(97.02, 38.8) * mm, "end": v(99.02, 42.26) * mm});
            skLineSegment(sketch, "E324", {"start": v(105.13, 38.73) * mm, "end": v(115.13, 56.05) * mm});
            skLineSegment(sketch, "E325", {"start": v(109.02, 59.58) * mm, "end": v(111.02, 63.04) * mm});
            skLineSegment(sketch, "E326", {"start": v(111.02, 63.04) * mm, "end": v(66.75, 88.6) * mm});
            skLineSegment(sketch, "E327", {"start": v(253.88, -207.54) * mm, "end": v(249.88, -207.54) * mm});
            skLineSegment(sketch, "E328", {"start": v(249.88, -207.54) * mm, "end": v(249.88, -215.54) * mm});
            skLineSegment(sketch, "E329", {"start": v(249.88, -215.54) * mm, "end": v(253.88, -215.54) * mm});
            skLineSegment(sketch, "E330", {"start": v(253.88, -215.54) * mm, "end": v(253.88, -207.54) * mm});
            skLineSegment(sketch, "E331", {"start": v(99.02, 42.26) * mm, "end": v(105.13, 38.73) * mm});
            skLineSegment(sketch, "E332", {"start": v(109.02, 59.58) * mm, "end": v(115.13, 56.05) * mm});
            skCircle(sketch, "E333", {"center": v(116.51, 43.7) * mm, "radius": 2 * mm});
            skArc(sketch, "E334", {"start": v(100.99, -19.2) * mm, "mid": v(121.34, -123.67) * mm, "end": v(201.64, -193.53) * mm});
            skArc(sketch, "E335", {"start": v(326.1, -193.53) * mm, "mid": v(406.41, -123.67) * mm, "end": v(426.76, -19.2) * mm});
            skLineSegment(sketch, "E336", {"start": v(253.88, -225.96) * mm, "end": v(253.88, -218.91) * mm});
            skLineSegment(sketch, "E337", {"start": v(273.88, -218.91) * mm, "end": v(273.88, -225.96) * mm});
            skCircle(sketch, "E338", {"center": v(263.88, -211.54) * mm, "radius": 2 * mm});
            skLineSegment(sketch, "E339", {"start": v(428.73, 42.26) * mm, "end": v(422.62, 38.73) * mm});
            skLineSegment(sketch, "E340", {"start": v(412.63, 56.05) * mm, "end": v(418.73, 59.58) * mm});
            skCircle(sketch, "E341", {"center": v(411.24, 43.7) * mm, "radius": 2 * mm});
            skCircle(sketch, "E342", {"center": v(263.88, -41.38) * mm, "radius": 2.5 * mm});
            skLineSegment(sketch, "E343", {"start": v(263.88, -41.38) * mm, "end": v(263.88, 185.62) * mm, "construction": true});
            skLineSegment(sketch, "E344", {"start": v(251.88, -167.66) * mm, "end": v(251.88, -156.9) * mm, "construction": true});
            skLineSegment(sketch, "E345", {"start": v(275.88, -167.66) * mm, "end": v(275.88, -156.9) * mm, "construction": true});
            skLineSegment(sketch, "E346.trimOffspring", {"start": v(275.88, -136.9) * mm, "end": v(275.88, -126.16) * mm, "construction": true});
            skLineSegment(sketch, "E347.trimOffspring", {"start": v(251.88, -136.9) * mm, "end": v(251.88, -126.16) * mm, "construction": true});
            skLineSegment(sketch, "E348.trimOffspring", {"start": v(275.88, -106.16) * mm, "end": v(275.88, -95.4) * mm, "construction": true});
            skLineSegment(sketch, "E349.trimOffspring", {"start": v(251.88, -106.16) * mm, "end": v(251.88, -95.4) * mm, "construction": true});
            skCircle(sketch, "E350", {"center": v(251.88, -162.28) * mm, "radius": 2 * mm});
            skCircle(sketch, "E351", {"center": v(275.88, -162.28) * mm, "radius": 2 * mm});
            skCircle(sketch, "E352", {"center": v(251.88, -131.53) * mm, "radius": 2 * mm});
            skCircle(sketch, "E353", {"center": v(275.88, -131.53) * mm, "radius": 2 * mm});
            skCircle(sketch, "E354", {"center": v(251.88, -100.78) * mm, "radius": 2 * mm});
            skCircle(sketch, "E355", {"center": v(275.88, -100.78) * mm, "radius": 2 * mm});
            skLineSegment(sketch, "E356", {"start": v(316.67, -24.75) * mm, "end": v(325.98, -19.38) * mm, "construction": true});
            skLineSegment(sketch, "E357", {"start": v(304.67, -3.97) * mm, "end": v(313.98, 1.4) * mm, "construction": true});
            skLineSegment(sketch, "E358.trimOffspring", {"start": v(331.3, 11.4) * mm, "end": v(340.6, 16.78) * mm, "construction": true});
            skLineSegment(sketch, "E359.trimOffspring", {"start": v(343.3, -9.38) * mm, "end": v(352.6, -4) * mm, "construction": true});
            skLineSegment(sketch, "E360.trimOffspring", {"start": v(369.93, 6) * mm, "end": v(379.24, 11.37) * mm, "construction": true});
            skLineSegment(sketch, "E361.trimOffspring", {"start": v(357.93, 26.78) * mm, "end": v(367.24, 32.16) * mm, "construction": true});
            skCircle(sketch, "E362", {"center": v(321.32, -22.07) * mm, "radius": 2 * mm});
            skCircle(sketch, "E363", {"center": v(309.32, -1.28) * mm, "radius": 2 * mm});
            skCircle(sketch, "E364", {"center": v(347.95, -6.7) * mm, "radius": 2 * mm});
            skCircle(sketch, "E365", {"center": v(335.95, 14.1) * mm, "radius": 2 * mm});
            skCircle(sketch, "E366", {"center": v(374.58, 8.68) * mm, "radius": 2 * mm});
            skCircle(sketch, "E367", {"center": v(362.58, 29.47) * mm, "radius": 2 * mm});
            skLineSegment(sketch, "E368", {"start": v(211.08, -24.75) * mm, "end": v(201.77, -19.38) * mm, "construction": true});
            skLineSegment(sketch, "E369", {"start": v(160.51, 32.16) * mm, "end": v(169.82, 26.78) * mm, "construction": true});
            skLineSegment(sketch, "E370.trimOffspring", {"start": v(157.82, 6) * mm, "end": v(148.51, 11.37) * mm, "construction": true});
            skLineSegment(sketch, "E371.trimOffspring", {"start": v(184.45, -9.38) * mm, "end": v(175.14, -4) * mm, "construction": true});
            skLineSegment(sketch, "E372.trimOffspring", {"start": v(213.77, 1.4) * mm, "end": v(223.08, -3.97) * mm, "construction": true});
            skLineSegment(sketch, "E373.trimOffspring", {"start": v(187.14, 16.78) * mm, "end": v(196.45, 11.4) * mm, "construction": true});
            skCircle(sketch, "E374", {"center": v(153.17, 8.68) * mm, "radius": 2 * mm});
            skCircle(sketch, "E375", {"center": v(165.17, 29.47) * mm, "radius": 2 * mm});
            skCircle(sketch, "E376", {"center": v(191.8, 14.1) * mm, "radius": 2 * mm});
            skCircle(sketch, "E377", {"center": v(179.8, -6.7) * mm, "radius": 2 * mm});
            skCircle(sketch, "E378", {"center": v(206.43, -22.07) * mm, "radius": 2 * mm});
            skCircle(sketch, "E379", {"center": v(218.43, -1.28) * mm, "radius": 2 * mm});
            skArc(sketch, "E380", {"start": v(-431.84, -33.47) * mm, "mid": v(-437.7, -19.32) * mm, "end": v(-451.84, -13.47) * mm});
            skArc(sketch, "E381", {"start": v(-451.84, -13.47) * mm, "mid": v(-461.8, -4.6) * mm, "end": v(-471.83, -13.37) * mm});
            skPoint(sketch, "E382", {"position": v(-471.84, -43.47) * mm});
            skLineSegment(sketch, "E383", {"start": v(-471.84, -53.47) * mm, "end": v(-431.84, -53.47) * mm});
            skPoint(sketch, "E384.orphan", {"position": v(-431.84, -43.47) * mm});
            skCircle(sketch, "E385", {"center": v(-461.84, -43.47) * mm, "radius": 2 * mm});
            skCircle(sketch, "E386", {"center": v(-445.87, -43.47) * mm, "radius": 2 * mm});
            skCircle(sketch, "E387", {"center": v(-461.84, -13.46) * mm, "radius": 2 * mm});
            skCircle(sketch, "E388", {"center": v(-461.84, -23.47) * mm, "radius": 2 * mm});
            skCircle(sketch, "E389", {"center": v(-443.84, -25.56) * mm, "radius": 1.5 * mm});
            skLineSegment(sketch, "E390", {"start": v(-325, 302.96) * mm, "end": v(-297, 302.96) * mm});
            skLineSegment(sketch, "E391", {"start": v(-311, 302.96) * mm, "end": v(-311, 289.9) * mm, "construction": true});
            skLineSegment(sketch, "E392.MirrorCS", {"start": v(-309.17, 291.44) * mm, "end": v(-309.17, 294.44) * mm});
            skLineSegment(sketch, "E393.MirrorCS", {"start": v(-300.95, 291.44) * mm, "end": v(-300.95, 287.57) * mm});
            skLineSegment(sketch, "E394.MirrorCS", {"start": v(-303.94, 291.45) * mm, "end": v(-300.95, 291.44) * mm});
            skLineSegment(sketch, "E395.MirrorCS", {"start": v(-303.94, 289.45) * mm, "end": v(-303.94, 291.45) * mm});
            skLineSegment(sketch, "E396.MirrorCS", {"start": v(-307.14, 291.44) * mm, "end": v(-307.14, 289.44) * mm});
            skLineSegment(sketch, "E397.MirrorCS", {"start": v(-300.95, 294.44) * mm, "end": v(-300.95, 298.32) * mm});
            skLineSegment(sketch, "E398.MirrorCS", {"start": v(-303.94, 296.45) * mm, "end": v(-303.94, 294.44) * mm});
            skLineSegment(sketch, "E399.MirrorCS", {"start": v(-303.94, 294.44) * mm, "end": v(-300.95, 294.44) * mm});
            skLineSegment(sketch, "E400.MirrorCS", {"start": v(-307.14, 294.44) * mm, "end": v(-307.14, 296.44) * mm});
            skLineSegment(sketch, "E401", {"start": v(-325, 282.96) * mm, "end": v(-297, 282.96) * mm});
            skLineSegment(sketch, "E402", {"start": v(-325, 302.96) * mm, "end": v(-325, 282.96) * mm});
            skLineSegment(sketch, "E403.right", {"start": v(-297, 302.96) * mm, "end": v(-297, 282.96) * mm});
            skLineSegment(sketch, "E404", {"start": v(-300.95, 287.57) * mm, "end": v(-297, 287.57) * mm});
            skLineSegment(sketch, "E405", {"start": v(-300.95, 298.32) * mm, "end": v(-297, 298.32) * mm});
            skLineSegment(sketch, "E406.left", {"start": v(-307.14, 296.44) * mm, "end": v(-307.14, 296.45) * mm});
            skLineSegment(sketch, "E406.right", {"start": v(-303.94, 289.44) * mm, "end": v(-303.94, 289.45) * mm});
            skLineSegment(sketch, "E407", {"start": v(-321.05, 287.57) * mm, "end": v(-325, 287.57) * mm});
            skLineSegment(sketch, "E408", {"start": v(-307.14, 289.44) * mm, "end": v(-303.94, 289.45) * mm});
            skLineSegment(sketch, "E409", {"start": v(-309.17, 291.44) * mm, "end": v(-307.14, 291.44) * mm});
            skLineSegment(sketch, "E410", {"start": v(-309.17, 294.44) * mm, "end": v(-307.14, 294.44) * mm});
            skLineSegment(sketch, "E411", {"start": v(-307.14, 296.45) * mm, "end": v(-303.94, 296.45) * mm});
            skLineSegment(sketch, "E412.right", {"start": v(-307.14, 291.44) * mm, "end": v(-307.14, 294.44) * mm});
            skLineSegment(sketch, "E413.bottom", {"start": v(-307.14, 289.44) * mm, "end": v(-303.94, 289.44) * mm});
            skLineSegment(sketch, "E413.left", {"start": v(-307.14, 289.44) * mm, "end": v(-307.14, 296.45) * mm});
            skLineSegment(sketch, "E413.right", {"start": v(-303.94, 289.44) * mm, "end": v(-303.94, 296.45) * mm});
            skLineSegment(sketch, "E414.bottom", {"start": v(-303.94, 291.45) * mm, "end": v(-300.95, 291.45) * mm});
            skLineSegment(sketch, "E414.left", {"start": v(-303.94, 291.45) * mm, "end": v(-303.94, 294.44) * mm});
            skLineSegment(sketch, "E414.right", {"start": v(-300.95, 291.45) * mm, "end": v(-300.95, 294.44) * mm});
            skCircle(sketch, "E415", {"center": v(336.36, 147) * mm, "radius": 1.75 * mm});
            skCircle(sketch, "E416", {"center": v(336.36, 197) * mm, "radius": 1.75 * mm});
            skLineSegment(sketch, "E417", {"start": v(300.35, 144.9) * mm, "end": v(300.65, 185.62) * mm});
            skLineSegment(sketch, "E418.MirrorCS", {"start": v(202.45, 185.62) * mm, "end": v(300.65, 185.62) * mm});
            skLineSegment(sketch, "E419.MirrorCS", {"start": v(300.35, 144.9) * mm, "end": v(202.15, 144.9) * mm});
            skLineSegment(sketch, "E420", {"start": v(202.45, 185.62) * mm, "end": v(202.15, 144.9) * mm});
            skCircle(sketch, "E421", {"center": v(191.17, 147) * mm, "radius": 1.75 * mm});
            skCircle(sketch, "E422", {"center": v(191.36, 196.94) * mm, "radius": 1.75 * mm});
            skCircle(sketch, "E423.MirrorC", {"center": v(326.05, 168.86) * mm, "radius": 10 * mm});
            skLineSegment(sketch, "E424", {"start": v(336.36, 147) * mm, "end": v(191.17, 147) * mm, "construction": true});
            skLineSegment(sketch, "E425", {"start": v(263.76, 147) * mm, "end": v(263.76, 168.23) * mm, "construction": true});
            skLineSegment(sketch, "E426.bottom", {"start": v(175.63, 212.62) * mm, "end": v(352.12, 212.62) * mm});
            skLineSegment(sketch, "E426.left", {"start": v(175.63, 212.62) * mm, "end": v(175.63, 128.15) * mm});
            skLineSegment(sketch, "E427", {"start": v(175.63, 128.15) * mm, "end": v(131.72, 88.6) * mm});
            skLineSegment(sketch, "E428.MirrorCS", {"start": v(352.12, 128.15) * mm, "end": v(396.03, 88.6) * mm});
            skLineSegment(sketch, "E429", {"start": v(352.12, 128.15) * mm, "end": v(352.12, 212.62) * mm});
            skLineSegment(sketch, "E430.trimOffspring", {"start": v(396.03, 88.6) * mm, "end": v(461, 88.6) * mm});
            skCircle(sketch, "E431", {"center": v(-11.84, 227.96) * mm, "radius": 2 * mm});
            skLineSegment(sketch, "E432", {"start": v(33.49, 217.95) * mm, "end": v(19.49, 193.7) * mm});
            skPoint(sketch, "E433.orphan", {"position": v(31.49, 214.49) * mm});
            skLineSegment(sketch, "E434", {"start": v(2.16, 272.22) * mm, "end": v(-25.84, 272.22) * mm});
            skPoint(sketch, "E435.orphan", {"position": v(-1.84, 272.22) * mm});
            skLineSegment(sketch, "E436", {"start": v(-43.17, 193.7) * mm, "end": v(-57.17, 217.95) * mm});
            skPoint(sketch, "E437.orphan", {"position": v(-45.17, 197.17) * mm});
            skLineSegment(sketch, "E438", {"start": v(16.49, 195.43) * mm, "end": v(30.49, 219.68) * mm});
            skLineSegment(sketch, "E439", {"start": v(-25.84, 268.75) * mm, "end": v(2.16, 268.75) * mm});
            skLineSegment(sketch, "E440", {"start": v(-40.17, 195.43) * mm, "end": v(-54.17, 219.68) * mm});
            skCircle(sketch, "E441", {"center": v(263.88, -41.38) * mm, "radius": 150 * mm, "construction": true});
            skLineSegment(sketch, "E442.0", {"start": v(414.66, -190.58) * mm, "end": v(114.67, -192.16) * mm, "construction": true});
            skLineSegment(sketch, "E442.1", {"start": v(114.67, -192.16) * mm, "end": v(113.09, 107.83) * mm, "construction": true});
            skLineSegment(sketch, "E442.2", {"start": v(113.09, 107.83) * mm, "end": v(413.08, 109.41) * mm, "construction": true});
            skLineSegment(sketch, "E442.3", {"start": v(413.08, 109.41) * mm, "end": v(414.66, -190.58) * mm, "construction": true});
            skPoint(sketch, "E442.0.midPoint", {"position": v(264.66, -191.37) * mm});
            skSolve(sketch);
        }
        {
            var Q0;
            Q0=makeQuery(id+"F0.imprint","IMPRINT",FACE,{"disambiguationData":[TD([[makeQuery(id+"F0.imprint","IMPRINT",EDGE,{"derivedFrom":sQuery(id+"F0.wireOp",EDGE,"E2")}),1.0]])]});
            var Q1;
            Q1=makeQuery(id+"F0.imprint","IMPRINT",FACE,{"disambiguationData":[TD([[makeQuery(id+"F0.imprint","IMPRINT",EDGE,{"derivedFrom":sQuery(id+"F0.wireOp",EDGE,"E13")}),1.0]])]});
            var Q2;
            Q2=makeQuery(id+"F0.imprint","IMPRINT",FACE,{"disambiguationData":[TD([[makeQuery(id+"F0.imprint","IMPRINT",EDGE,{"derivedFrom":sQuery(id+"F0.wireOp",EDGE,"E0")}),1.0]])]});
            var Q3;
            Q3=makeQuery(id+"F0.imprint","IMPRINT",FACE,{"disambiguationData":[TD([[makeQuery(id+"F0.imprint","IMPRINT",EDGE,{"derivedFrom":sQuery(id+"F0.wireOp",EDGE,"E44")}),1.0]])]});
            var Q4;
            Q4=makeQuery(id+"F0.imprint","IMPRINT",FACE,{"disambiguationData":[TD([[makeQuery(id+"F0.imprint","IMPRINT",EDGE,{"derivedFrom":sQuery(id+"F0.wireOp",EDGE,"E17")}),-1.0]])]});
            var Q5;
            Q5=makeQuery(id+"F0.imprint","IMPRINT",FACE,{"disambiguationData":[TD([[makeQuery(id+"F0.imprint","IMPRINT",EDGE,{"derivedFrom":sQuery(id+"F0.wireOp",EDGE,"E191")}),-1.0]])]});
            var Q6;
            Q6=makeQuery(id+"F0.imprint","IMPRINT",FACE,{"disambiguationData":[TD([[makeQuery(id+"F0.imprint","IMPRINT",EDGE,{"derivedFrom":sQuery(id+"F0.wireOp",EDGE,"E188")}),-1.0]])]});
            var Q7;
            {var subQ0=sQuery(id+"F0.wireOp",EDGE,"E28");Q7=makeQuery(id+"F0.imprint","IMPRINT",FACE,{"disambiguationData":[TD([[makeQuery(id+"F0.imprint","IMPRINT",EDGE,{"derivedFrom":subQ0}),1.0]])]});}
            var Q8;
            {var subQ0=sQuery(id+"F0.wireOp",EDGE,"E23");Q8=makeQuery(id+"F0.imprint","IMPRINT",FACE,{"disambiguationData":[TD([[makeQuery(id+"F0.imprint","IMPRINT",EDGE,{"derivedFrom":subQ0}),1.0]])]});}
            var Q9;
            {var subQ0=sQuery(id+"F0.wireOp",EDGE,"E19");Q9=makeQuery(id+"F0.imprint","IMPRINT",FACE,{"disambiguationData":[TD([[makeQuery(id+"F0.imprint","IMPRINT",EDGE,{"derivedFrom":subQ0}),1.0]])]});}
            var Q10;
            {var subQ24=sQuery(id+"F0.wireOp",EDGE,"E19");Q10=makeQuery(id+"F0.imprint","IMPRINT",FACE,{"disambiguationData":[TD([[makeQuery(id+"F0.imprint","IMPRINT",EDGE,{"derivedFrom":subQ24}),-1.0]])]});}
            var Q11;
            {var subQ0=sQuery(id+"F0.wireOp",EDGE,"E41");Q11=makeQuery(id+"F0.imprint","IMPRINT",FACE,{"disambiguationData":[TD([[makeQuery(id+"F0.imprint","IMPRINT",EDGE,{"derivedFrom":subQ0}),1.0]])]});}
            var Q12;
            {var subQ6=sQuery(id+"F0.wireOp",EDGE,"E34");Q12=makeQuery(id+"F0.imprint","IMPRINT",FACE,{"disambiguationData":[TD([[makeQuery(id+"F0.imprint","IMPRINT",EDGE,{"derivedFrom":subQ6}),-1.0]])]});}
            var Q13;
            {var subQ0=sQuery(id+"F0.wireOp",EDGE,"E37");Q13=makeQuery(id+"F0.imprint","IMPRINT",FACE,{"disambiguationData":[TD([[makeQuery(id+"F0.imprint","IMPRINT",EDGE,{"derivedFrom":subQ0}),1.0]])]});}
            var Q14;
            {var subQ0=sQuery(id+"F0.wireOp",EDGE,"E32");Q14=makeQuery(id+"F0.imprint","IMPRINT",FACE,{"disambiguationData":[TD([[makeQuery(id+"F0.imprint","IMPRINT",EDGE,{"derivedFrom":subQ0}),1.0]])]});}
            var Q15;
            {var subQ4=sQuery(id+"F0.wireOp",EDGE,"E25");Q15=makeQuery(id+"F0.imprint","IMPRINT",FACE,{"disambiguationData":[TD([[makeQuery(id+"F0.imprint","IMPRINT",EDGE,{"derivedFrom":subQ4}),-1.0]])]});}
            var Q16;
            {var subQ26=sQuery(id+"F0.wireOp",EDGE,"E19");Q16=makeQuery(id+"F0.imprint","IMPRINT",FACE,{"disambiguationData":[TD([[makeQuery(id+"F0.imprint","IMPRINT",EDGE,{"derivedFrom":subQ26}),-1.0]])]});}
            var Q17;
            {var subQ0=sQuery(id+"F0.wireOp",EDGE,"E432");var subQ1=sQuery(id+"F0.wireOp",EDGE,"E24");var subQ2=makeQuery(id+"F0.imprint","INTERSECT",VERTEX,{"derivedFrom":[subQ1,subQ0]});Q17=makeQuery(id+"F0.imprint","IMPRINT",FACE,{"disambiguationData":[TD([[makeQuery(id+"F0.imprint","IMPRINT",EDGE,{"disambiguationData":[TD([[subQ2,1.0]])],"derivedFrom":subQ1}),-1.0]])]});}
            var Q18;
            {var subQ0=sQuery(id+"F0.wireOp",EDGE,"E23");Q18=makeQuery(id+"F0.imprint","IMPRINT",FACE,{"disambiguationData":[TD([[makeQuery(id+"F0.imprint","IMPRINT",EDGE,{"derivedFrom":subQ0}),1.0]])]});}
            var Q19;
            {var subQ0=sQuery(id+"F0.wireOp",EDGE,"E434");var subQ1=sQuery(id+"F0.wireOp",EDGE,"E18");var subQ2=makeQuery(id+"F0.imprint","INTERSECT",VERTEX,{"derivedFrom":[subQ1,subQ0]});Q19=makeQuery(id+"F0.imprint","IMPRINT",FACE,{"disambiguationData":[TD([[makeQuery(id+"F0.imprint","IMPRINT",EDGE,{"disambiguationData":[TD([[subQ2,-1.0]])],"derivedFrom":subQ1}),-1.0]])]});}
            var Q20;
            {var subQ0=sQuery(id+"F0.wireOp",EDGE,"E436");var subQ1=sQuery(id+"F0.wireOp",EDGE,"E33");var subQ2=makeQuery(id+"F0.imprint","INTERSECT",VERTEX,{"derivedFrom":[subQ1,subQ0]});Q20=makeQuery(id+"F0.imprint","IMPRINT",FACE,{"disambiguationData":[TD([[makeQuery(id+"F0.imprint","IMPRINT",EDGE,{"disambiguationData":[TD([[subQ2,1.0]])],"derivedFrom":subQ1}),-1.0]])]});}
            extrude(context, id + "F1", {"entities" : qUnion([Q0, Q1, Q2, Q3, Q4, Q5, Q6, Q7, Q8, Q9, Q10, Q11, Q12, Q13, Q14, Q15, Q16, Q17, Q18, Q19, Q20]), "depth" : 4 * mm});
        }
        {
            var Q0;
            Q0=qCreatedBy(makeId("Top.planeOp"),FACE);
            var sketch = newSketch(context, id + "F2", { "sketchPlane" : qUnion([Q0])});
            skCircle(sketch, "E443", {"center": v(-121.85, -375.87) * mm, "radius": 2 * mm});
            skCircle(sketch, "E444", {"center": v(-88.9, -375.87) * mm, "radius": 2 * mm});
            skCircle(sketch, "E445", {"center": v(-172.94, -424.4) * mm, "radius": 2 * mm});
            skCircle(sketch, "E446", {"center": v(-156.46, -395.85) * mm, "radius": 2 * mm});
            skCircle(sketch, "E447", {"center": v(-156.46, -355.9) * mm, "radius": 2 * mm});
            skCircle(sketch, "E448", {"center": v(-172.94, -327.35) * mm, "radius": 2 * mm});
            skCircle(sketch, "E449", {"center": v(-144.92, -375.87) * mm, "radius": 2 * mm});
            skLineSegment(sketch, "E450", {"start": v(-185.74, -319.52) * mm, "end": v(-173.32, -312.35) * mm});
            skArc(sketch, "E451", {"start": v(-162.26, -315.04) * mm, "mid": v(-128.44, -347.33) * mm, "end": v(-83.57, -360.47) * mm});
            skLineSegment(sketch, "E452", {"start": v(-173.32, -439.4) * mm, "end": v(-185.74, -432.23) * mm});
            skArc(sketch, "E453", {"start": v(-83.57, -391.28) * mm, "mid": v(-128.44, -404.42) * mm, "end": v(-162.26, -436.71) * mm});
            skLineSegment(sketch, "E454", {"start": v(-75.7, -368.7) * mm, "end": v(-75.7, -383.04) * mm});
            skArc(sketch, "E455", {"start": v(-188.94, -421.3) * mm, "mid": v(-177.88, -375.87) * mm, "end": v(-188.94, -330.44) * mm});
            skArc(sketch, "E456", {"start": v(-75.7, -368.7) * mm, "mid": v(-77.99, -363.01) * mm, "end": v(-83.57, -360.47) * mm});
            skArc(sketch, "E457", {"start": v(-83.57, -391.28) * mm, "mid": v(-77.99, -388.74) * mm, "end": v(-75.7, -383.04) * mm});
            skArc(sketch, "E458", {"start": v(-173.32, -439.4) * mm, "mid": v(-167.25, -440.27) * mm, "end": v(-162.26, -436.71) * mm});
            skArc(sketch, "E459", {"start": v(-188.94, -421.3) * mm, "mid": v(-189.53, -427.41) * mm, "end": v(-185.74, -432.23) * mm});
            skArc(sketch, "E460", {"start": v(-185.74, -319.52) * mm, "mid": v(-189.53, -324.34) * mm, "end": v(-188.94, -330.44) * mm});
            skArc(sketch, "E461", {"start": v(-162.26, -315.04) * mm, "mid": v(-167.25, -311.48) * mm, "end": v(-173.32, -312.35) * mm});
            skCircle(sketch, "E462", {"center": v(-132, -364.33) * mm, "radius": 1.5 * mm});
            skCircle(sketch, "E463", {"center": v(-132, -387.4) * mm, "radius": 1.5 * mm});
            skCircle(sketch, "E464", {"center": v(-101, -364.33) * mm, "radius": 1.5 * mm});
            skCircle(sketch, "E465", {"center": v(-101, -387.4) * mm, "radius": 1.5 * mm});
            skCircle(sketch, "E466", {"center": v(-141.48, -392.7) * mm, "radius": 1.5 * mm});
            skCircle(sketch, "E467", {"center": v(-161.45, -381.16) * mm, "radius": 1.5 * mm});
            skCircle(sketch, "E468", {"center": v(-156.98, -419.54) * mm, "radius": 1.5 * mm});
            skCircle(sketch, "E469", {"center": v(-176.95, -408) * mm, "radius": 1.5 * mm});
            skCircle(sketch, "E470", {"center": v(-161.33, -370.57) * mm, "radius": 1.5 * mm});
            skCircle(sketch, "E471", {"center": v(-141.36, -359.04) * mm, "radius": 1.5 * mm});
            skCircle(sketch, "E472", {"center": v(-176.83, -343.72) * mm, "radius": 1.5 * mm});
            skCircle(sketch, "E473", {"center": v(-156.86, -332.2) * mm, "radius": 1.5 * mm});
            skSolve(sketch);
        }
        {
            var Q0;
            Q0=makeQuery(id+"F2.imprint","IMPRINT",FACE,{"disambiguationData":[TD([[makeQuery(id+"F2.imprint","IMPRINT",EDGE,{"derivedFrom":sQuery(id+"F2.wireOp",EDGE,"E469")}),-1.0]])]});
            var Q1;
            Q1=makeQuery(id+"F2.imprint","IMPRINT",FACE,{"disambiguationData":[TD([[makeQuery(id+"F2.imprint","IMPRINT",EDGE,{"derivedFrom":sQuery(id+"F2.wireOp",EDGE,"E467")}),-1.0]])]});
            var Q2;
            Q2=makeQuery(id+"F2.imprint","IMPRINT",FACE,{"disambiguationData":[TD([[makeQuery(id+"F2.imprint","IMPRINT",EDGE,{"derivedFrom":sQuery(id+"F2.wireOp",EDGE,"E470")}),-1.0]])]});
            var Q3;
            Q3=makeQuery(id+"F2.imprint","IMPRINT",FACE,{"disambiguationData":[TD([[makeQuery(id+"F2.imprint","IMPRINT",EDGE,{"derivedFrom":sQuery(id+"F2.wireOp",EDGE,"E462")}),-1.0]])]});
            var Q4;
            Q4=makeQuery(id+"F2.imprint","IMPRINT",FACE,{"disambiguationData":[TD([[makeQuery(id+"F2.imprint","IMPRINT",EDGE,{"derivedFrom":sQuery(id+"F2.wireOp",EDGE,"E463")}),-1.0]])]});
            var Q5;
            Q5=makeQuery(id+"F2.imprint","IMPRINT",FACE,{"disambiguationData":[TD([[makeQuery(id+"F2.imprint","IMPRINT",EDGE,{"derivedFrom":sQuery(id+"F2.wireOp",EDGE,"E466")}),-1.0]])]});
            var Q6;
            Q6=makeQuery(id+"F2.imprint","IMPRINT",FACE,{"disambiguationData":[TD([[makeQuery(id+"F2.imprint","IMPRINT",EDGE,{"derivedFrom":sQuery(id+"F2.wireOp",EDGE,"E464")}),-1.0]])]});
            var Q7;
            Q7=makeQuery(id+"F2.imprint","IMPRINT",FACE,{"disambiguationData":[TD([[makeQuery(id+"F2.imprint","IMPRINT",EDGE,{"derivedFrom":sQuery(id+"F2.wireOp",EDGE,"E465")}),-1.0]])]});
            var Q8;
            Q8=makeQuery(id+"F2.imprint","IMPRINT",FACE,{"disambiguationData":[TD([[makeQuery(id+"F2.imprint","IMPRINT",EDGE,{"derivedFrom":sQuery(id+"F2.wireOp",EDGE,"E443")}),1.0]])]});
            var Q9;
            Q9=makeQuery(id+"F2.imprint","IMPRINT",FACE,{"disambiguationData":[TD([[makeQuery(id+"F2.imprint","IMPRINT",EDGE,{"derivedFrom":sQuery(id+"F2.wireOp",EDGE,"E471")}),-1.0]])]});
            var Q10;
            Q10=makeQuery(id+"F2.imprint","IMPRINT",FACE,{"disambiguationData":[TD([[makeQuery(id+"F2.imprint","IMPRINT",EDGE,{"derivedFrom":sQuery(id+"F2.wireOp",EDGE,"E468")}),-1.0]])]});
            var Q11;
            Q11=makeQuery(id+"F2.imprint","IMPRINT",FACE,{"disambiguationData":[TD([[makeQuery(id+"F2.imprint","IMPRINT",EDGE,{"derivedFrom":sQuery(id+"F2.wireOp",EDGE,"E472")}),-1.0]])]});
            var Q12;
            Q12=makeQuery(id+"F2.imprint","IMPRINT",FACE,{"disambiguationData":[TD([[makeQuery(id+"F2.imprint","IMPRINT",EDGE,{"derivedFrom":sQuery(id+"F2.wireOp",EDGE,"E473")}),-1.0]])]});
            extrude(context, id + "F3", {"entities" : qUnion([Q0, Q1, Q2, Q3, Q4, Q5, Q6, Q7, Q8, Q9, Q10, Q11, Q12]), "depth" : 4 * mm});
        }
        {
            var Q0;
            Q0=qCreatedBy(makeId("Top.planeOp"),FACE);
            var sketch = newSketch(context, id + "F4", { "sketchPlane" : qUnion([Q0])});
            skCircle(sketch, "E474", {"center": v(-7.91, 32.96) * mm, "radius": 5.9 * mm});
            skCircle(sketch, "E475", {"center": v(-37.91, -19) * mm, "radius": 5.9 * mm});
            skCircle(sketch, "E476", {"center": v(7.91, 32.96) * mm, "radius": 5.9 * mm});
            skCircle(sketch, "E477", {"center": v(37.91, -19) * mm, "radius": 5.9 * mm});
            skCircle(sketch, "E478", {"center": v(30, -32.7) * mm, "radius": 5.9 * mm});
            skCircle(sketch, "E479", {"center": v(-30, -32.7) * mm, "radius": 5.9 * mm});
            skLineSegment(sketch, "E480", {"start": v(-48.2, -22.75) * mm, "end": v(-38.4, -39.75) * mm});
            skLineSegment(sketch, "E481", {"start": v(-31.47, -43.75) * mm, "end": v(31.47, -43.75) * mm});
            skLineSegment(sketch, "E482", {"start": v(38.4, -39.75) * mm, "end": v(48.2, -22.75) * mm});
            skLineSegment(sketch, "E483", {"start": v(48.2, -14.75) * mm, "end": v(16.74, 39.75) * mm});
            skLineSegment(sketch, "E484", {"start": v(9.81, 43.75) * mm, "end": v(-9.81, 43.75) * mm});
            skLineSegment(sketch, "E485", {"start": v(-16.74, 39.75) * mm, "end": v(-48.2, -14.75) * mm});
            skArc(sketch, "E486", {"start": v(-48.2, -14.75) * mm, "mid": v(-49.28, -18.75) * mm, "end": v(-48.2, -22.75) * mm});
            skArc(sketch, "E487", {"start": v(-9.81, 43.75) * mm, "mid": v(-13.81, 42.68) * mm, "end": v(-16.74, 39.75) * mm});
            skArc(sketch, "E488", {"start": v(16.74, 39.75) * mm, "mid": v(13.81, 42.68) * mm, "end": v(9.81, 43.75) * mm});
            skArc(sketch, "E489", {"start": v(48.2, -22.75) * mm, "mid": v(49.28, -18.75) * mm, "end": v(48.2, -14.75) * mm});
            skArc(sketch, "E490", {"start": v(31.47, -43.75) * mm, "mid": v(35.47, -42.68) * mm, "end": v(38.4, -39.75) * mm});
            skArc(sketch, "E491", {"start": v(-38.4, -39.75) * mm, "mid": v(-35.47, -42.68) * mm, "end": v(-31.47, -43.75) * mm});
            skCircle(sketch, "E492", {"center": v(0, -6.25) * mm, "radius": 15 * mm});
            skCircle(sketch, "E493", {"center": v(0, -34.25) * mm, "radius": 6 * mm});
            skCircle(sketch, "E494", {"center": v(0, 16.25) * mm, "radius": 1.5 * mm});
            skCircle(sketch, "E495", {"center": v(-19.49, -17.5) * mm, "radius": 1.5 * mm});
            skCircle(sketch, "E496", {"center": v(19.49, -17.5) * mm, "radius": 1.5 * mm});
            skSolve(sketch);
        }
        {
            var Q0;
            Q0=makeQuery(id+"F4.imprint","IMPRINT",FACE,{"disambiguationData":[TD([[makeQuery(id+"F4.imprint","IMPRINT",EDGE,{"derivedFrom":sQuery(id+"F4.wireOp",EDGE,"E474")}),1.0]])]});
            extrude(context, id + "F5", {"entities" : qUnion([Q0]), "depth" : 4 * mm});
        }
        {
            var Q0;
            Q0=qCreatedBy(makeId("Top.planeOp"),FACE);
            var sketch = newSketch(context, id + "F6", { "sketchPlane" : qUnion([Q0])});
            skArc(sketch, "E497", {"start": v(-997.16, -154.63) * mm, "mid": v(-1022.13, -149.45) * mm, "end": v(-1047.52, -147) * mm});
            skLineSegment(sketch, "E498", {"start": v(-1057.52, -382.78) * mm, "end": v(-1057.52, 221.6) * mm, "construction": true});
            skArc(sketch, "E499.0", {"start": v(-993.6, -145.23) * mm, "mid": v(-1057.6, -136.78) * mm, "end": v(-1121.58, -145.27) * mm});
            skPoint(sketch, "E500", {"position": v(-1119.52, -155.07) * mm});
            skPoint(sketch, "E501", {"position": v(-1121.58, -145.27) * mm});
            skPoint(sketch, "E502", {"position": v(-993.6, -145.23) * mm});
            skPoint(sketch, "E503", {"position": v(-997.16, -154.63) * mm});
            skLineSegment(sketch, "E504", {"start": v(-993.6, -145.23) * mm, "end": v(-997.16, -154.63) * mm});
            skLineSegment(sketch, "E505", {"start": v(-1119.52, -155.07) * mm, "end": v(-1121.58, -145.27) * mm});
            skLineSegment(sketch, "E506", {"start": v(-1057.52, -146.78) * mm, "end": v(-1057.52, -162) * mm, "construction": true});
            skLineSegment(sketch, "E507", {"start": v(-1057.52, -162) * mm, "end": v(-1067.52, -162) * mm});
            skLineSegment(sketch, "E508", {"start": v(-1067.52, -162) * mm, "end": v(-1067.52, -147) * mm});
            skLineSegment(sketch, "E509.MirrorCS", {"start": v(-1057.52, -162) * mm, "end": v(-1047.52, -162) * mm});
            skLineSegment(sketch, "E510.MirrorCS", {"start": v(-1047.52, -162) * mm, "end": v(-1047.52, -147) * mm});
            skArc(sketch, "E511.trimOffspring", {"start": v(-1067.52, -147) * mm, "mid": v(-1093.74, -149.58) * mm, "end": v(-1119.52, -155.07) * mm});
            skSolve(sketch);
        }
        {
            var Q0;
            Q0=makeQuery(id+"F6.imprint","IMPRINT",FACE,{"disambiguationData":[TD([[makeQuery(id+"F6.imprint","IMPRINT",EDGE,{"derivedFrom":sQuery(id+"F6.wireOp",EDGE,"E497")}),-1.0]])]});
            extrude(context, id + "F7", {"entities" : qUnion([Q0]), "depth" : 40 * mm});
        }
        {
            var Q0;
            Q0=qCreatedBy(makeId("Top.planeOp"),FACE);
            var sketch = newSketch(context, id + "F8", { "sketchPlane" : qUnion([Q0])});
            skCircle(sketch, "E512", {"center": v(-987.28, -479.12) * mm, "radius": 251 * mm});
            skCircle(sketch, "E513.0", {"center": v(-987.28, -479.12) * mm, "radius": 254 * mm});
            skLineSegment(sketch, "E514", {"start": v(-987.28, -479.12) * mm, "end": v(-733.28, -479.12) * mm});
            skLineSegment(sketch, "E515", {"start": v(-987.28, -479.12) * mm, "end": v(-1054.07, -724.18) * mm});
            skSolve(sketch);
        }
        {
            var Q0;
            {var subQ0=sQuery(id+"F8.wireOp",EDGE,"E514");var subQ1=sQuery(id+"F8.wireOp",EDGE,"E512");var subQ2=makeQuery(id+"F8.imprint","INTERSECT",VERTEX,{"derivedFrom":[subQ1,subQ0]});Q0=makeQuery(id+"F8.imprint","IMPRINT",FACE,{"disambiguationData":[TD([[makeQuery(id+"F8.imprint","IMPRINT",EDGE,{"disambiguationData":[TD([[subQ2,-1.0]])],"derivedFrom":subQ1}),-1.0]])]});}
            extrude(context, id + "F9", {"entities" : qUnion([Q0]), "depth" : 700 * mm});
        }
        {
            var Q0;
            Q0=qCreatedBy(makeId("Top.planeOp"),FACE);
            var sketch = newSketch(context, id + "F10", { "sketchPlane" : qUnion([Q0])});
            skLineSegment(sketch, "E516.top", {"start": v(881.7, -354.58) * mm, "end": v(901.7, -354.58) * mm});
            skLineSegment(sketch, "E516.left", {"start": v(881.7, -334.58) * mm, "end": v(881.7, -354.58) * mm});
            skLineSegment(sketch, "E516.right", {"start": v(901.7, -337.7) * mm, "end": v(901.7, -354.58) * mm});
            skLineSegment(sketch, "E517", {"start": v(891.7, -368.03) * mm, "end": v(891.7, -133.03) * mm, "construction": true});
            skLineSegment(sketch, "E518", {"start": v(901.7, -344.58) * mm, "end": v(915.7, -344.58) * mm, "construction": true});
            skLineSegment(sketch, "E519", {"start": v(881.7, -344.58) * mm, "end": v(867.7, -344.58) * mm, "construction": true});
            skCircle(sketch, "E520", {"center": v(867.7, -344.58) * mm, "radius": 2 * mm});
            skCircle(sketch, "E521", {"center": v(915.7, -344.58) * mm, "radius": 2 * mm});
            skArc(sketch, "E522", {"start": v(725.96, 33.57) * mm, "mid": v(688.19, -15.53) * mm, "end": v(664.56, -72.8) * mm});
            skLineSegment(sketch, "E523", {"start": v(881.7, -334.58) * mm, "end": v(881.7, -318.58) * mm});
            skLineSegment(sketch, "E524", {"start": v(901.7, -318.58) * mm, "end": v(901.7, -337.7) * mm});
            skArc(sketch, "E525", {"start": v(901.7, -318.58) * mm, "mid": v(891.7, -308.58) * mm, "end": v(881.7, -318.58) * mm});
            skLineSegment(sketch, "E526.1.0", {"start": v(1043.74, -45.25) * mm, "end": v(891.7, -133.03) * mm, "construction": true});
            skLineSegment(sketch, "E526.1.1", {"start": v(1063.95, -22.04) * mm, "end": v(1075.88, -15.15) * mm});
            skLineSegment(sketch, "E526.1.2", {"start": v(1088.58, -30.91) * mm, "end": v(1078.58, -13.6) * mm});
            skLineSegment(sketch, "E526.1.3", {"start": v(1071.25, -40.91) * mm, "end": v(1088.58, -30.91) * mm});
            skLineSegment(sketch, "E526.1.4", {"start": v(1071.25, -40.91) * mm, "end": v(1057.4, -48.91) * mm});
            skLineSegment(sketch, "E526.1.5", {"start": v(1069.92, -18.6) * mm, "end": v(1062.92, -6.47) * mm, "construction": true});
            skCircle(sketch, "E526.1.6", {"center": v(1086.92, -48.04) * mm, "radius": 2 * mm});
            skCircle(sketch, "E526.1.7", {"center": v(1062.92, -6.47) * mm, "radius": 2 * mm});
            skLineSegment(sketch, "E526.1.8", {"start": v(1047.4, -31.6) * mm, "end": v(1063.95, -22.04) * mm});
            skArc(sketch, "E526.1.9", {"start": v(1047.4, -31.6) * mm, "mid": v(1043.74, -45.25) * mm, "end": v(1057.4, -48.91) * mm});
            skLineSegment(sketch, "E526.1.10", {"start": v(1079.92, -35.91) * mm, "end": v(1086.92, -48.04) * mm, "construction": true});
            skLineSegment(sketch, "E526.2.0", {"start": v(739.67, -45.25) * mm, "end": v(891.7, -133.03) * mm, "construction": true});
            skLineSegment(sketch, "E526.2.1", {"start": v(709.46, -39.36) * mm, "end": v(697.52, -32.47) * mm});
            skLineSegment(sketch, "E526.2.2", {"start": v(704.83, -13.6) * mm, "end": v(694.83, -30.91) * mm});
            skLineSegment(sketch, "E526.2.3", {"start": v(722.15, -23.6) * mm, "end": v(704.83, -13.6) * mm});
            skLineSegment(sketch, "E526.2.4", {"start": v(722.15, -23.6) * mm, "end": v(736, -31.6) * mm});
            skLineSegment(sketch, "E526.2.5", {"start": v(703.5, -35.91) * mm, "end": v(696.5, -48.04) * mm, "construction": true});
            skCircle(sketch, "E526.2.6", {"center": v(720.5, -6.47) * mm, "radius": 2 * mm});
            skCircle(sketch, "E526.2.7", {"center": v(696.5, -48.04) * mm, "radius": 2 * mm});
            skLineSegment(sketch, "E526.2.8", {"start": v(726, -48.91) * mm, "end": v(709.46, -39.36) * mm});
            skArc(sketch, "E526.2.9", {"start": v(726, -48.91) * mm, "mid": v(739.67, -45.25) * mm, "end": v(736, -31.6) * mm});
            skLineSegment(sketch, "E526.2.10", {"start": v(713.5, -18.6) * mm, "end": v(720.5, -6.47) * mm, "construction": true});
            skPoint(sketch, "E527.0.midPoint", {"position": v(1122.12, 0) * mm});
            skPoint(sketch, "E528.0.midPoint", {"position": v(1088.15, -19.61) * mm});
            skLineSegment(sketch, "E529", {"start": v(953.11, -359.86) * mm, "end": v(1118.85, -72.8) * mm});
            skPoint(sketch, "E530.orphan", {"position": v(891.7, 320.64) * mm});
            skPoint(sketch, "E531.orphan", {"position": v(498.81, -359.86) * mm});
            skLineSegment(sketch, "E532", {"start": v(664.56, -72.8) * mm, "end": v(830.3, -359.86) * mm});
            skLineSegment(sketch, "E533", {"start": v(725.96, 33.57) * mm, "end": v(1057.44, 33.57) * mm});
            skArc(sketch, "E534.trimOffspring", {"start": v(830.3, -359.86) * mm, "mid": v(891.7, -368.03) * mm, "end": v(953.11, -359.86) * mm});
            skArc(sketch, "E535.trimOffspring", {"start": v(1118.85, -72.8) * mm, "mid": v(1095.22, -15.53) * mm, "end": v(1057.44, 33.57) * mm});
            skLineSegment(sketch, "E536", {"start": v(703.5, -35.91) * mm, "end": v(713.5, -18.6) * mm, "construction": true});
            skLineSegment(sketch, "E537", {"start": v(1069.92, -18.6) * mm, "end": v(1079.92, -35.91) * mm, "construction": true});
            skLineSegment(sketch, "E538", {"start": v(881.7, -344.58) * mm, "end": v(901.7, -344.58) * mm, "construction": true});
            skCircle(sketch, "E539", {"center": v(891.7, -344.58) * mm, "radius": 2.5 * mm});
            skCircle(sketch, "E540", {"center": v(708.5, -27.25) * mm, "radius": 2.5 * mm});
            skCircle(sketch, "E541", {"center": v(1074.92, -27.25) * mm, "radius": 2.5 * mm});
            skArc(sketch, "E542", {"start": v(830.3, -359.86) * mm, "mid": v(831.52, -167.78) * mm, "end": v(664.56, -72.8) * mm, "construction": true});
            skArc(sketch, "E543", {"start": v(1118.85, -72.8) * mm, "mid": v(951.9, -167.78) * mm, "end": v(953.11, -359.86) * mm, "construction": true});
            skArc(sketch, "E544", {"start": v(725.96, 33.57) * mm, "mid": v(891.7, -63.53) * mm, "end": v(1057.44, 33.57) * mm, "construction": true});
            skPoint(sketch, "E545.orphan", {"position": v(891.7, -308.58) * mm});
            skLineSegment(sketch, "E546", {"start": v(881.7, -354.58) * mm, "end": v(877.7, -354.58) * mm});
            skLineSegment(sketch, "E547", {"start": v(877.7, -354.58) * mm, "end": v(877.7, -334.58) * mm});
            skLineSegment(sketch, "E548", {"start": v(877.7, -334.58) * mm, "end": v(881.7, -334.58) * mm});
            skLineSegment(sketch, "E549.MirrorCS", {"start": v(905.7, -334.58) * mm, "end": v(901.7, -334.58) * mm});
            skLineSegment(sketch, "E550.MirrorCS", {"start": v(905.7, -354.58) * mm, "end": v(905.7, -334.58) * mm});
            skLineSegment(sketch, "E551.MirrorCS", {"start": v(901.7, -354.58) * mm, "end": v(905.7, -354.58) * mm});
            skLineSegment(sketch, "E552.1.0", {"start": v(1073.25, -44.38) * mm, "end": v(1071.25, -40.91) * mm});
            skLineSegment(sketch, "E552.1.1", {"start": v(1090.58, -34.38) * mm, "end": v(1073.25, -44.38) * mm});
            skLineSegment(sketch, "E552.1.2", {"start": v(1088.58, -30.91) * mm, "end": v(1090.58, -34.38) * mm});
            skLineSegment(sketch, "E552.1.3", {"start": v(1078.58, -13.6) * mm, "end": v(1076.58, -10.13) * mm});
            skLineSegment(sketch, "E552.1.4", {"start": v(1076.58, -10.13) * mm, "end": v(1059.25, -20.13) * mm});
            skLineSegment(sketch, "E552.1.5", {"start": v(1059.25, -20.13) * mm, "end": v(1061.25, -23.6) * mm});
            skLineSegment(sketch, "E552.2.0", {"start": v(724.15, -20.13) * mm, "end": v(722.15, -23.6) * mm});
            skLineSegment(sketch, "E552.2.1", {"start": v(706.83, -10.13) * mm, "end": v(724.15, -20.13) * mm});
            skLineSegment(sketch, "E552.2.2", {"start": v(704.83, -13.6) * mm, "end": v(706.83, -10.13) * mm});
            skLineSegment(sketch, "E552.2.3", {"start": v(694.83, -30.91) * mm, "end": v(692.83, -34.38) * mm});
            skLineSegment(sketch, "E552.2.4", {"start": v(692.83, -34.38) * mm, "end": v(710.15, -44.38) * mm});
            skLineSegment(sketch, "E552.2.5", {"start": v(710.15, -44.38) * mm, "end": v(712.15, -40.91) * mm});
            skSolve(sketch);
        }
        {
            var Q0;
            Q0=makeQuery(id+"F10.imprint","IMPRINT",FACE,{"disambiguationData":[TD([[makeQuery(id+"F10.imprint","IMPRINT",EDGE,{"derivedFrom":sQuery(id+"F10.wireOp",EDGE,"E516.top")}),-1.0]])]});
            extrude(context, id + "F11", {"entities" : qUnion([Q0]), "depth" : 10 * mm});
        }
        {
            var Q0;
            Q0=qCreatedBy(makeId("Top.planeOp"),FACE);
            var sketch = newSketch(context, id + "F12", { "sketchPlane" : qUnion([Q0])});
            skLineSegment(sketch, "E553.bottom", {"start": v(366.14, -374.13) * mm, "end": v(374.14, -374.13) * mm});
            skLineSegment(sketch, "E553.top", {"start": v(352.57, -329.13) * mm, "end": v(374.14, -329.13) * mm});
            skLineSegment(sketch, "E553.right", {"start": v(374.14, -374.13) * mm, "end": v(374.14, -349.13) * mm});
            skLineSegment(sketch, "E554", {"start": v(366.14, -374.13) * mm, "end": v(366.14, -329.13) * mm, "construction": true});
            skCircle(sketch, "E555", {"center": v(366.14, -366.13) * mm, "radius": 3.5 * mm, "construction": true});
            skCircle(sketch, "E556", {"center": v(366.14, -356.13) * mm, "radius": 3.5 * mm, "construction": true});
            skCircle(sketch, "E557", {"center": v(366.14, -339.13) * mm, "radius": 2 * mm});
            skPoint(sketch, "E558", {"position": v(366.14, -349.13) * mm});
            skLineSegment(sketch, "E559", {"start": v(366.14, -339.13) * mm, "end": v(354.08, -339.13) * mm, "construction": true});
            skCircle(sketch, "E560", {"center": v(354.08, -339.13) * mm, "radius": 2 * mm});
            skLineSegment(sketch, "E561", {"start": v(347.57, -334.13) * mm, "end": v(347.57, -344.13) * mm});
            skPoint(sketch, "E562.visualSharp", {"position": v(347.57, -329.13) * mm});
            skArc(sketch, "E562.filletArc", {"start": v(352.57, -329.13) * mm, "mid": v(349.03, -330.6) * mm, "end": v(347.57, -334.13) * mm});
            skLineSegment(sketch, "E563", {"start": v(355.46, -349.13) * mm, "end": v(352.57, -349.13) * mm});
            skPoint(sketch, "E564", {"position": v(356.14, -349.13) * mm});
            skLineSegment(sketch, "E565", {"start": v(356.14, -349.81) * mm, "end": v(356.14, -369.13) * mm});
            skLineSegment(sketch, "E566", {"start": v(361.14, -374.13) * mm, "end": v(366.14, -374.13) * mm});
            skPoint(sketch, "E567.visualSharp", {"position": v(347.57, -349.13) * mm});
            skArc(sketch, "E567.filletArc", {"start": v(347.57, -344.13) * mm, "mid": v(349.03, -347.67) * mm, "end": v(352.57, -349.13) * mm});
            skArc(sketch, "E568.filletArc", {"start": v(356.14, -349.81) * mm, "mid": v(355.94, -349.33) * mm, "end": v(355.46, -349.13) * mm});
            skPoint(sketch, "E569.visualSharp", {"position": v(356.14, -374.13) * mm});
            skArc(sketch, "E569.filletArc", {"start": v(356.14, -369.13) * mm, "mid": v(357.6, -372.67) * mm, "end": v(361.14, -374.13) * mm});
            skCircle(sketch, "E570", {"center": v(366.14, -366.13) * mm, "radius": 1.5 * mm});
            skCircle(sketch, "E571", {"center": v(366.14, -356.13) * mm, "radius": 1.5 * mm});
            skPoint(sketch, "E572", {"position": v(366.14, -362.63) * mm});
            skPoint(sketch, "E573", {"position": v(366.14, -352.63) * mm});
            skCircle(sketch, "E574", {"center": v(359.67, -358.13) * mm, "radius": 3.28 * mm, "construction": true});
            skLineSegment(sketch, "E575", {"start": v(366.14, -362.63) * mm, "end": v(349.95, -362.63) * mm, "construction": true});
            skCircle(sketch, "E576", {"center": v(359.67, -358.13) * mm, "radius": 1.5 * mm});
            skLineSegment(sketch, "E577.bottom", {"start": v(374.14, -349.13) * mm, "end": v(376.64, -349.13) * mm});
            skLineSegment(sketch, "E577.top", {"start": v(374.14, -329.13) * mm, "end": v(376.64, -329.13) * mm});
            skLineSegment(sketch, "E577.right", {"start": v(376.64, -349.13) * mm, "end": v(376.64, -329.13) * mm});
            skLineSegment(sketch, "E578", {"start": v(376.64, -329.13) * mm, "end": v(386.64, -329.13) * mm, "construction": true});
            skSolve(sketch);
        }
        {
            var Q0;
            Q0=qCreatedBy(makeId("Top.planeOp"),FACE);
            var sketch = newSketch(context, id + "F13", { "sketchPlane" : qUnion([Q0])});
            skCircle(sketch, "E579", {"center": v(261.23, -550.54) * mm, "radius": 1.65 * mm});
            skCircle(sketch, "E580", {"center": v(276.78, -535) * mm, "radius": 11.05 * mm});
            skCircle(sketch, "E581", {"center": v(292.33, -550.49) * mm, "radius": 1.65 * mm});
            skCircle(sketch, "E582", {"center": v(292.33, -519.27) * mm, "radius": 1.65 * mm});
            skCircle(sketch, "E583", {"center": v(261.23, -519.27) * mm, "radius": 1.65 * mm});
            skLineSegment(sketch, "E584.bottom", {"start": v(260.78, -494) * mm, "end": v(292.79, -494) * mm});
            skPoint(sketch, "E585", {"position": v(297.79, -555.97) * mm});
            skLineSegment(sketch, "E586", {"start": v(297.79, -550.97) * mm, "end": v(297.79, -514) * mm});
            skLineSegment(sketch, "E587", {"start": v(292.79, -555.97) * mm, "end": v(260.78, -555.97) * mm});
            skPoint(sketch, "E588.visualSharp", {"position": v(255.78, -555.97) * mm});
            skArc(sketch, "E588.filletArc", {"start": v(255.78, -550.97) * mm, "mid": v(257.25, -554.5) * mm, "end": v(260.78, -555.97) * mm});
            skPoint(sketch, "E589.visualSharp", {"position": v(297.79, -494) * mm});
            skLineSegment(sketch, "E589.filletArc", {"start": v(292.79, -494) * mm, "end": v(292.79, -494) * mm});
            skPoint(sketch, "E590.visualSharp", {"position": v(255.78, -494) * mm});
            skArc(sketch, "E591.filletArc", {"start": v(292.79, -555.97) * mm, "mid": v(296.32, -554.5) * mm, "end": v(297.79, -550.97) * mm});
            skLineSegment(sketch, "E592", {"start": v(276.78, -591.46) * mm, "end": v(276.78, -555.97) * mm, "construction": true});
            skCircle(sketch, "E593", {"center": v(540.18, -430.49) * mm, "radius": 1.65 * mm});
            skPoint(sketch, "E594.visualSharp", {"position": v(503.63, -467.2) * mm});
            skPoint(sketch, "E595", {"position": v(255.78, -504) * mm});
            skPoint(sketch, "E596", {"position": v(265.78, -494) * mm});
            skCircle(sketch, "E597", {"center": v(265.78, -504) * mm, "radius": 2 * mm});
            skCircle(sketch, "E598.MirrorC", {"center": v(287.79, -504) * mm, "radius": 2 * mm});
            skLineSegment(sketch, "E599.bottom", {"start": v(255.78, -494) * mm, "end": v(253.28, -494) * mm});
            skLineSegment(sketch, "E599.top", {"start": v(255.78, -514) * mm, "end": v(253.28, -514) * mm});
            skLineSegment(sketch, "E599.right", {"start": v(253.28, -494) * mm, "end": v(253.28, -514) * mm});
            skLineSegment(sketch, "E600", {"start": v(255.78, -494) * mm, "end": v(260.78, -494) * mm});
            skLineSegment(sketch, "E601.MirrorCS", {"start": v(297.79, -494) * mm, "end": v(292.79, -494) * mm});
            skLineSegment(sketch, "E602.MirrorCS", {"start": v(297.79, -494) * mm, "end": v(301.79, -494) * mm});
            skLineSegment(sketch, "E603.MirrorCS", {"start": v(301.79, -494) * mm, "end": v(301.79, -514) * mm});
            skLineSegment(sketch, "E604.MirrorCS", {"start": v(297.79, -514) * mm, "end": v(301.79, -514) * mm});
            skLineSegment(sketch, "E605.trimOffspring", {"start": v(255.78, -514) * mm, "end": v(255.78, -550.97) * mm});
            skPoint(sketch, "E606.orphan", {"position": v(300.29, -514) * mm});
            skPoint(sketch, "E607.orphan", {"position": v(300.29, -494) * mm});
            skSolve(sketch);
        }
        {
            var Q0;
            Q0=makeQuery(id+"F12.imprint","IMPRINT",FACE,{"disambiguationData":[TD([[makeQuery(id+"F12.imprint","IMPRINT",EDGE,{"derivedFrom":sQuery(id+"F12.wireOp",EDGE,"E553.bottom")}),1.0]])]});
            var Q1;
            Q1=makeQuery(id+"F13.imprint","IMPRINT",FACE,{"disambiguationData":[TD([[makeQuery(id+"F13.imprint","IMPRINT",EDGE,{"derivedFrom":sQuery(id+"F13.wireOp",EDGE,"E579")}),-1.0]])]});
            extrude(context, id + "F14", {"entities" : qUnion([Q0, Q1]), "depth" : 4 * mm});
        }
    });
